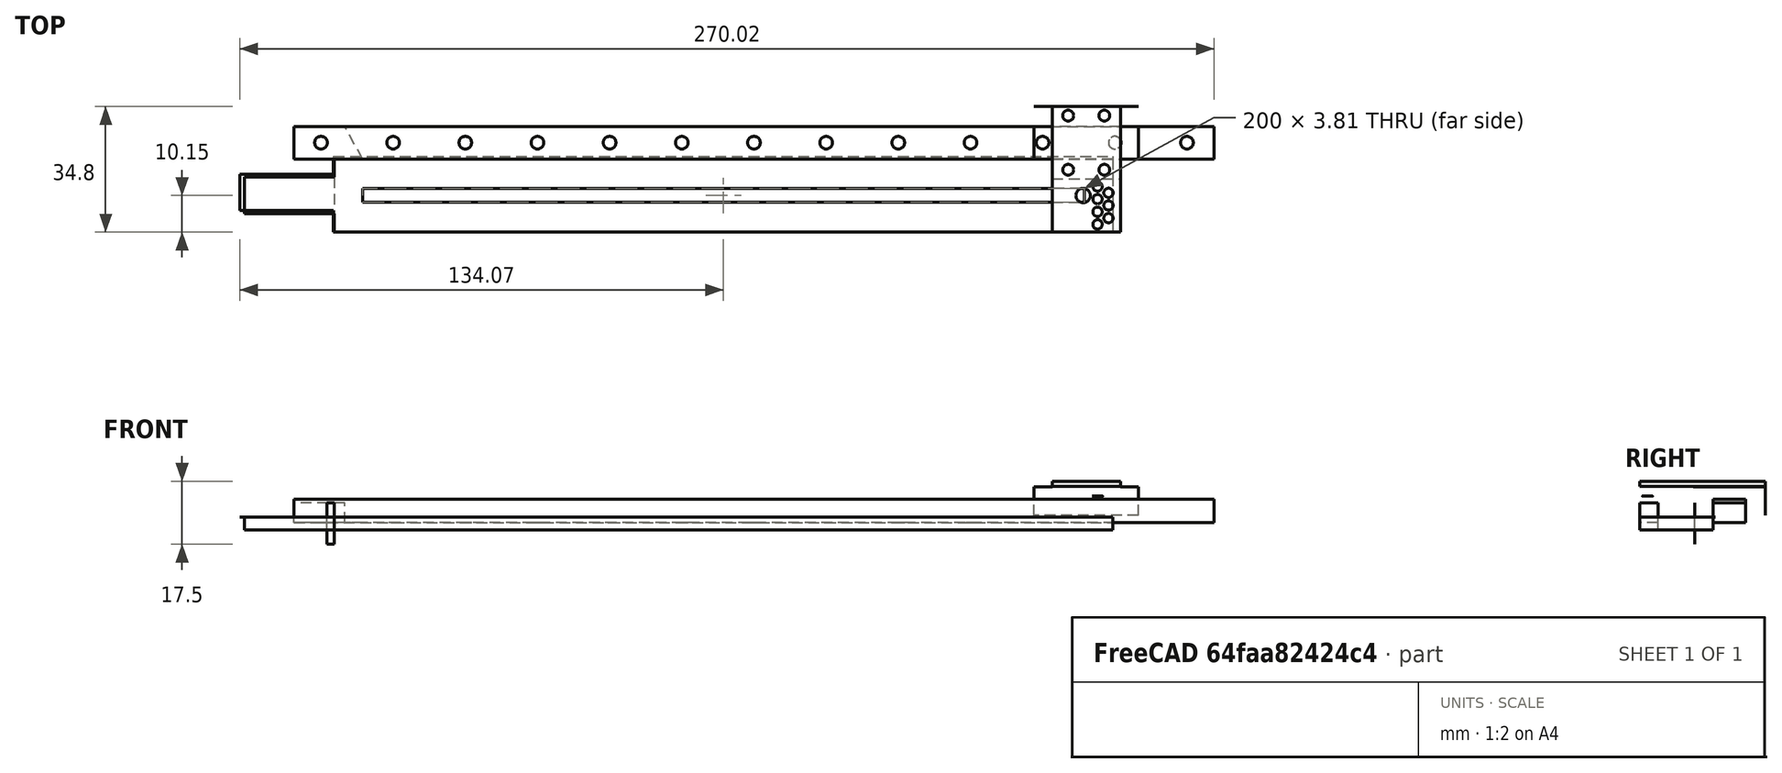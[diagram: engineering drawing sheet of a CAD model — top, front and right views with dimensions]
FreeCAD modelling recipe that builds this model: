
FCSTD DOCUMENT  (FreeCAD 0.21R33668 +26 (Git))
Label: v9
License: All rights reserved
LicenseURL: http://en.wikipedia.org/wiki/All_rights_reserved
objects: App::FeaturePython×73, Part::FeaturePython×54, App::Link×13
note: 53 computed .brp shape members not serialized (recipe doc carries the construction recipe); baked Part::Feature solids carry a one-line shape summary decoded from their .brp
EXTERNAL_REF file=parts/MG/mgn9c_13.FCStd obj=Body
EXTERNAL_REF file=parts/MG/mgn9c_slide.FCStd obj=Body001
EXTERNAL_REF file=parts/MagnetoPot/MagnetoPot.FCStd obj=Body
EXTERNAL_REF file=parts/NormalConnectorWithPin.FCStd obj=Body
EXTERNAL_REF file=parts/OmniballConnector/OmniballConnector_7945.FCStd obj=Body
EXTERNAL_REF file=parts/MagnetoPot/FlexBoard/FlexBoard_CAD.FCStd obj=Board_2da8
EXTERNAL_REF file=parts/BaseMagnetoPot.FCStd obj=Body

FEATURE [App::Link] Link  label="Rail"
  LinkedObject = -> <external parts/MG/mgn9c_13.FCStd>#Body
  _LinkOwner = 1895
FEATURE [App::Link] Link001  label="Slide"
  LinkPlacement = pos=(205.149,-5.5,2) rot=(0,0,1;0rad)
  LinkedObject = -> <external parts/MG/mgn9c_slide.FCStd>#Body001
  Placement = pos=(205.149,-5.5,2) rot=(0,0,1;0rad)
  _LinkOwner = 1895
FEATURE [App::Link] Link003  label="MP1_L_0200_103_5_ST"
  LinkPlacement = pos=(11.12,-20.3,-2) rot=(0,0,1;0rad)
  LinkedObject = -> <external parts/MagnetoPot/MagnetoPot.FCStd>#Body
  Placement = pos=(11.12,-20.3,-2) rot=(0,0,1;0rad)
  _LinkOwner = 1895
FEATURE [App::Link] Link005  label="SlideConnector"
  LinkPlacement = pos=(205.149,-5.5,2) rot=(0,0,1;0rad)
  LinkedObject = -> <external parts/NormalConnectorWithPin.FCStd>#Body
  Placement = pos=(205.149,-5.5,2) rot=(0,0,1;0rad)
  _LinkOwner = 1895
FEATURE [App::Link] Link006  label="7945"
  LinkPlacement = pos=(222.722,-18.15,8.1374) rot=(0,1,0;3.14159rad)
  LinkedObject = -> <external parts/OmniballConnector/OmniballConnector_7945.FCStd>#Body
  Placement = pos=(222.722,-18.15,8.1374) rot=(0,1,0;3.14159rad)
  _LinkOwner = 1895
FEATURE [App::Link] Link007  label="7945001"
  LinkPlacement = pos=(222.722,-14.65,8.1374) rot=(-1,0,0;3.14159rad)
  LinkedObject = -> <external parts/OmniballConnector/OmniballConnector_7945.FCStd>#Body
  Placement = pos=(222.722,-14.65,8.1374) rot=(-1,0,0;3.14159rad)
  _LinkOwner = 1895
FEATURE [App::Link] Link008  label="7945002"
  LinkPlacement = pos=(222.722,-11.15,8.1374) rot=(-1,0,0;3.14159rad)
  LinkedObject = -> <external parts/OmniballConnector/OmniballConnector_7945.FCStd>#Body
  Placement = pos=(222.722,-11.15,8.1374) rot=(-1,0,0;3.14159rad)
  _LinkOwner = 1895
FEATURE [App::Link] Link009  label="7945003"
  LinkPlacement = pos=(222.722,-7.65,8.1374) rot=(-1,0,0;3.14159rad)
  LinkedObject = -> <external parts/OmniballConnector/OmniballConnector_7945.FCStd>#Body
  Placement = pos=(222.722,-7.65,8.1374) rot=(-1,0,0;3.14159rad)
  _LinkOwner = 1895
FEATURE [App::Link] Link010  label="7945004"
  LinkPlacement = pos=(225.753,-16.4,8.1374) rot=(1,0,0;3.14159rad)
  LinkedObject = -> <external parts/OmniballConnector/OmniballConnector_7945.FCStd>#Body
  Placement = pos=(225.753,-16.4,8.1374) rot=(1,0,0;3.14159rad)
  _LinkOwner = 1895
FEATURE [App::Link] Link011  label="7945005"
  LinkPlacement = pos=(225.753,-9.4,8.1374) rot=(1,0,0;3.14159rad)
  LinkedObject = -> <external parts/OmniballConnector/OmniballConnector_7945.FCStd>#Body
  Placement = pos=(225.753,-9.4,8.1374) rot=(1,0,0;3.14159rad)
  _LinkOwner = 1895
FEATURE [App::Link] Link012  label="7945006"
  LinkPlacement = pos=(225.753,-12.9,8.1374) rot=(1,0,0;3.14159rad)
  LinkedObject = -> <external parts/OmniballConnector/OmniballConnector_7945.FCStd>#Body
  Placement = pos=(225.753,-12.9,8.1374) rot=(1,0,0;3.14159rad)
  _LinkOwner = 1895
FEATURE [App::Link] Link013  label="FlexBoard"
  LinkPlacement = pos=(25.38,-8.9,1.615) rot=(0,0,1;0rad)
  LinkedObject = -> <external parts/MagnetoPot/FlexBoard/FlexBoard_CAD.FCStd>#Board_2da8
  Placement = pos=(25.38,-8.9,1.615) rot=(0,0,1;0rad)
  _LinkOwner = 1895
FEATURE [App::Link] Link014  label="BaseMagentoPot"
  LinkPlacement = pos=(2.94885e-11,-3.58486e-11,-7.69447e-11) rot=(0,0,1;0rad)
  LinkedObject = -> <external parts/BaseMagnetoPot.FCStd>#Body
  Placement = pos=(2.94885e-11,-3.58486e-11,-7.69447e-11) rot=(0,0,1;0rad)
  _LinkOwner = 1895
FEATURE [Part::FeaturePython] Parts  # WARN: FeaturePython — macro-defined, semantics opaque (R4)
  Group = -> [Link,Link001,Link003,Link005,Link006,Link007,Link008,Link009,Link010,Link011,Link012,Link013,Link014]
  GroupMode = 0
FEATURE [App::FeaturePython] ElementLink  label="_Element"  # link proxy (typed FeaturePython)
  LinkTransform = true
  LinkedObject = -> _Element
  _Parent = -> Constraint
FEATURE [App::FeaturePython] Constraint  label="Locked"  # WARN: FeaturePython — macro-defined, semantics opaque (R4)
  Disabled = false
  Group = -> [ElementLink]
  _ConstraintType = 0
  _Parent = -> Constraints
FEATURE [App::FeaturePython] ElementLink001  label="_Element001"  # link proxy (typed FeaturePython)
  LinkTransform = true
  LinkedObject = -> _Element001
  _Parent = -> Constraint001
FEATURE [App::FeaturePython] ElementLink002  label="_Element002"  # link proxy (typed FeaturePython)
  LinkTransform = true
  LinkedObject = -> _Element002
  _Parent = -> Constraint001
FEATURE [App::FeaturePython] Constraint001  label="PlaneAlignment"  # WARN: FeaturePython — macro-defined, semantics opaque (R4)
  Angle = 0
  AnglePitch = 0
  AngleRoll = 0
  Cascade = false
  Disabled = false
  Group = -> [ElementLink001,ElementLink002]
  LockAngle = false
  _ConstraintType = 37
  _Parent = -> Constraints
FEATURE [App::FeaturePython] ElementLink003  label="_Element003"  # link proxy (typed FeaturePython)
  LinkTransform = true
  LinkedObject = -> _Element003
  _Parent = -> Constraint002
FEATURE [App::FeaturePython] ElementLink004  label="_Element"  # link proxy (typed FeaturePython)
  LinkTransform = true
  LinkedObject = -> _Element
  _Parent = -> Constraint002
FEATURE [App::FeaturePython] Constraint002  label="PlaneAlignment001"  # WARN: FeaturePython — macro-defined, semantics opaque (R4)
  Angle = 0
  AnglePitch = 0
  AngleRoll = 0
  Cascade = false
  Disabled = false
  Group = -> [ElementLink003,ElementLink004]
  LockAngle = false
  _ConstraintType = 37
  _Parent = -> Constraints
FEATURE [App::FeaturePython] ElementLink023  label="_Element020"  # link proxy (typed FeaturePython)
  LinkTransform = true
  LinkedObject = -> _Element020
  _Parent = -> Constraint012
FEATURE [App::FeaturePython] ElementLink024  label="_Element021"  # link proxy (typed FeaturePython)
  LinkTransform = true
  LinkedObject = -> _Element021
  _Parent = -> Constraint012
FEATURE [App::FeaturePython] Constraint012  label="PlaneAlignment011"  # WARN: FeaturePython — macro-defined, semantics opaque (R4)
  Angle = 0
  AnglePitch = 0
  AngleRoll = 0
  Cascade = false
  Disabled = false
  Group = -> [ElementLink023,ElementLink024]
  LockAngle = false
  _ConstraintType = 37
  _Parent = -> Constraints
FEATURE [App::FeaturePython] ElementLink025  label="_Element022"  # link proxy (typed FeaturePython)
  LinkTransform = true
  LinkedObject = -> _Element022
  _Parent = -> Constraint013
FEATURE [App::FeaturePython] ElementLink026  label="_Element023"  # link proxy (typed FeaturePython)
  LinkTransform = true
  LinkedObject = -> _Element023
  _Parent = -> Constraint013
FEATURE [App::FeaturePython] Constraint013  label="PlaneAlignment012"  # WARN: FeaturePython — macro-defined, semantics opaque (R4)
  Angle = 0
  AnglePitch = 0
  AngleRoll = 0
  Cascade = false
  Disabled = false
  Group = -> [ElementLink025,ElementLink026]
  LockAngle = false
  _ConstraintType = 37
  _Parent = -> Constraints
FEATURE [App::FeaturePython] ElementLink027  label="_Element024"  # link proxy (typed FeaturePython)
  LinkTransform = true
  LinkedObject = -> _Element024
  _Parent = -> Constraint014
FEATURE [App::FeaturePython] ElementLink028  label="_Element025"  # link proxy (typed FeaturePython)
  LinkTransform = true
  LinkedObject = -> _Element025
  _Parent = -> Constraint014
FEATURE [App::FeaturePython] Constraint014  label="PlaneAlignment013"  # WARN: FeaturePython — macro-defined, semantics opaque (R4)
  Angle = 0
  AnglePitch = 0
  AngleRoll = 0
  Cascade = false
  Disabled = false
  Group = -> [ElementLink027,ElementLink028]
  LockAngle = false
  _ConstraintType = 37
  _Parent = -> Constraints
FEATURE [App::FeaturePython] ElementLink029  label="_Element030"  # link proxy (typed FeaturePython)
  LinkTransform = true
  LinkedObject = -> _Element030
  _Parent = -> Constraint015
FEATURE [App::FeaturePython] ElementLink030  label="_Element031"  # link proxy (typed FeaturePython)
  LinkTransform = true
  LinkedObject = -> _Element031
  _Parent = -> Constraint015
FEATURE [App::FeaturePython] Constraint015  label="PlaneCoincident"  # WARN: FeaturePython — macro-defined, semantics opaque (R4)
  Angle = 0
  AnglePitch = 0
  AngleRoll = 0
  Cascade = false
  Disabled = false
  Group = -> [ElementLink029,ElementLink030]
  LockAngle = false
  Multiply = false
  OffsetX = 0
  OffsetY = 0
  _ConstraintType = 35
  _Parent = -> Constraints
FEATURE [App::FeaturePython] ElementLink031  label="_Element032"  # link proxy (typed FeaturePython)
  LinkTransform = true
  LinkedObject = -> _Element032
  _Parent = -> Constraint016
FEATURE [App::FeaturePython] ElementLink032  label="_Element033"  # link proxy (typed FeaturePython)
  LinkTransform = true
  LinkedObject = -> _Element033
  _Parent = -> Constraint016
FEATURE [App::FeaturePython] Constraint016  label="PlaneCoincident001"  # WARN: FeaturePython — macro-defined, semantics opaque (R4)
  Angle = 0
  AnglePitch = 0
  AngleRoll = 0
  Cascade = false
  Disabled = false
  Group = -> [ElementLink031,ElementLink032]
  LockAngle = false
  Multiply = false
  OffsetX = 0
  OffsetY = 0
  _ConstraintType = 35
  _Parent = -> Constraints
FEATURE [App::FeaturePython] ElementLink033  label="_Element034"  # link proxy (typed FeaturePython)
  LinkTransform = true
  LinkedObject = -> _Element034
  _Parent = -> Constraint017
FEATURE [App::FeaturePython] ElementLink034  label="_Element035"  # link proxy (typed FeaturePython)
  LinkTransform = true
  LinkedObject = -> _Element035
  _Parent = -> Constraint017
FEATURE [App::FeaturePython] Constraint017  label="PlaneCoincident002"  # WARN: FeaturePython — macro-defined, semantics opaque (R4)
  Angle = 0
  AnglePitch = 0
  AngleRoll = 0
  Cascade = false
  Disabled = false
  Group = -> [ElementLink033,ElementLink034]
  LockAngle = false
  Multiply = false
  OffsetX = 0
  OffsetY = 0
  _ConstraintType = 35
  _Parent = -> Constraints
FEATURE [App::FeaturePython] ElementLink035  label="_Element036"  # link proxy (typed FeaturePython)
  LinkTransform = true
  LinkedObject = -> _Element036
  _Parent = -> Constraint018
FEATURE [App::FeaturePython] ElementLink036  label="_Element037"  # link proxy (typed FeaturePython)
  LinkTransform = true
  LinkedObject = -> _Element037
  _Parent = -> Constraint018
FEATURE [App::FeaturePython] Constraint018  label="PlaneCoincident003"  # WARN: FeaturePython — macro-defined, semantics opaque (R4)
  Angle = 0
  AnglePitch = 0
  AngleRoll = 0
  Cascade = false
  Disabled = false
  Group = -> [ElementLink035,ElementLink036]
  LockAngle = false
  Multiply = false
  OffsetX = 0
  OffsetY = 0
  _ConstraintType = 35
  _Parent = -> Constraints
FEATURE [App::FeaturePython] ElementLink037  label="_Element038"  # link proxy (typed FeaturePython)
  LinkTransform = true
  LinkedObject = -> _Element038
  _Parent = -> Constraint019
FEATURE [App::FeaturePython] ElementLink038  label="_Element039"  # link proxy (typed FeaturePython)
  LinkTransform = true
  LinkedObject = -> _Element039
  _Parent = -> Constraint019
FEATURE [App::FeaturePython] Constraint019  label="PlaneCoincident004"  # WARN: FeaturePython — macro-defined, semantics opaque (R4)
  Angle = 0
  AnglePitch = 0
  AngleRoll = 0
  Cascade = false
  Disabled = false
  Group = -> [ElementLink037,ElementLink038]
  LockAngle = false
  Multiply = false
  OffsetX = 0
  OffsetY = 0
  _ConstraintType = 35
  _Parent = -> Constraints
FEATURE [App::FeaturePython] ElementLink039  label="_Element040"  # link proxy (typed FeaturePython)
  LinkTransform = true
  LinkedObject = -> _Element040
  _Parent = -> Constraint020
FEATURE [App::FeaturePython] ElementLink040  label="_Element041"  # link proxy (typed FeaturePython)
  LinkTransform = true
  LinkedObject = -> _Element041
  _Parent = -> Constraint020
FEATURE [App::FeaturePython] Constraint020  label="PlaneCoincident005"  # WARN: FeaturePython — macro-defined, semantics opaque (R4)
  Angle = 0
  AnglePitch = 0
  AngleRoll = 0
  Cascade = false
  Disabled = false
  Group = -> [ElementLink039,ElementLink040]
  LockAngle = false
  Multiply = false
  OffsetX = 0
  OffsetY = 0
  _ConstraintType = 35
  _Parent = -> Constraints
FEATURE [App::FeaturePython] ElementLink041  label="_Element042"  # link proxy (typed FeaturePython)
  LinkTransform = true
  LinkedObject = -> _Element042
  _Parent = -> Constraint021
FEATURE [App::FeaturePython] ElementLink042  label="_Element043"  # link proxy (typed FeaturePython)
  LinkTransform = true
  LinkedObject = -> _Element043
  _Parent = -> Constraint021
FEATURE [App::FeaturePython] Constraint021  label="PlaneCoincident006"  # WARN: FeaturePython — macro-defined, semantics opaque (R4)
  Angle = 0
  AnglePitch = 0
  AngleRoll = 0
  Cascade = false
  Disabled = false
  Group = -> [ElementLink041,ElementLink042]
  LockAngle = false
  Multiply = false
  OffsetX = 0
  OffsetY = 0
  _ConstraintType = 35
  _Parent = -> Constraints
FEATURE [App::FeaturePython] Constraints  # WARN: FeaturePython — macro-defined, semantics opaque (R4)
  Group = -> [Constraint,Constraint001,Constraint002,Constraint012,Constraint013,Constraint014,Constraint015,Constraint016,Constraint017,Constraint018,Constraint019,Constraint020,Constraint021,Constraint024,Constraint026,Constraint027,Constraint028,Constraint029,Constraint030,Constraint031,Constraint032,Constraint033,Constraint034,Constraint035]
  _Version = 1
FEATURE [Part::FeaturePython] _Element  # link proxy (typed FeaturePython)
  Detach = false
  LinkTransform = true
  LinkedObject = -> Link [LinearPattern.Face5]
  _Parent = -> Elements
FEATURE [Part::FeaturePython] _Element001  # link proxy (typed FeaturePython)
  Detach = false
  LinkTransform = true
  LinkedObject = -> Link001 [Pocket003.Face12]
  _Parent = -> Elements
FEATURE [Part::FeaturePython] _Element002  # link proxy (typed FeaturePython)
  Detach = false
  LinkTransform = true
  LinkedObject = -> Link [LinearPattern.Face6]
  _Parent = -> Elements
FEATURE [Part::FeaturePython] _Element003  # link proxy (typed FeaturePython)
  Detach = false
  LinkTransform = true
  LinkedObject = -> Link001 [Pocket003.Face11]
  _Parent = -> Elements
FEATURE [Part::FeaturePython] _Element005  # link proxy (typed FeaturePython)
  Detach = false
  LinkTransform = true
  LinkedObject = -> Link [LinearPattern.Face2]
  _Parent = -> Elements
FEATURE [Part::FeaturePython] _Element008  # link proxy (typed FeaturePython)
  Detach = false
  LinkTransform = true
  LinkedObject = -> Link [LinearPattern.Face4]
  _Parent = -> Elements
FEATURE [Part::FeaturePython] _Element009  # link proxy (typed FeaturePython)
  Detach = false
  LinkTransform = true
  LinkedObject = -> Link003 [Pad.Face13]
  _Parent = -> Elements
FEATURE [Part::FeaturePython] _Element012  # link proxy (typed FeaturePython)
  Detach = false
  LinkTransform = true
  LinkedObject = -> Link003 [Pad.Face5]
  _Parent = -> Elements
FEATURE [Part::FeaturePython] _Element013  # link proxy (typed FeaturePython)
  Detach = false
  LinkTransform = true
  LinkedObject = -> Link003 [Pad.Face8]
  _Parent = -> Elements
FEATURE [Part::FeaturePython] _Element016  # link proxy (typed FeaturePython)
  Detach = false
  LinkTransform = true
  LinkedObject = -> Link003 [Pad.Face14]
  _Parent = -> Elements
FEATURE [Part::FeaturePython] _Element020  # link proxy (typed FeaturePython)
  Detach = false
  LinkTransform = true
  LinkedObject = -> Link005 [Pocket002.Face4]
  _Parent = -> Elements
FEATURE [Part::FeaturePython] _Element021  # link proxy (typed FeaturePython)
  Detach = false
  LinkTransform = true
  LinkedObject = -> Link001 [Pocket003.Face6]
  _Parent = -> Elements
FEATURE [Part::FeaturePython] _Element022  # link proxy (typed FeaturePython)
  Detach = false
  LinkTransform = true
  LinkedObject = -> Link005 [Pocket002.Face1]
  _Parent = -> Elements
FEATURE [Part::FeaturePython] _Element023  # link proxy (typed FeaturePython)
  Detach = false
  LinkTransform = true
  LinkedObject = -> Link001 [Pocket003.Face14]
  _Parent = -> Elements
FEATURE [Part::FeaturePython] _Element024  # link proxy (typed FeaturePython)
  Detach = false
  LinkTransform = true
  LinkedObject = -> Link005 [Pocket002.Face2]
  _Parent = -> Elements
FEATURE [Part::FeaturePython] _Element025  # link proxy (typed FeaturePython)
  Detach = false
  LinkTransform = true
  LinkedObject = -> Link001 [Pocket003.Face7]
  _Parent = -> Elements
FEATURE [Part::FeaturePython] _Element026  # link proxy (typed FeaturePython)
  Detach = false
  LinkTransform = true
  LinkedObject = -> Link006 [Revolution.Face3]
  _Parent = -> Elements
FEATURE [Part::FeaturePython] _Element027  # link proxy (typed FeaturePython)
  Detach = false
  LinkTransform = true
  LinkedObject = -> Link005 [Pocket002.Face5]
  _Parent = -> Elements
FEATURE [Part::FeaturePython] _Element028  # link proxy (typed FeaturePython)
  Detach = false
  LinkTransform = true
  LinkedObject = -> Link006 [Revolution.Vertex2]
  _Parent = -> Elements
FEATURE [Part::FeaturePython] _Element029  # link proxy (typed FeaturePython)
  Detach = false
  LinkTransform = true
  LinkedObject = -> Link005 [Pocket002.Edge20]
  _Parent = -> Elements
FEATURE [Part::FeaturePython] _Element030  # link proxy (typed FeaturePython)
  Detach = false
  LinkTransform = true
  LinkedObject = -> Link006 [Revolution.Edge3]
  _Parent = -> Elements
FEATURE [Part::FeaturePython] _Element031  # link proxy (typed FeaturePython)
  Detach = false
  LinkTransform = true
  LinkedObject = -> Link005 [Pocket003.Edge40]
  _Parent = -> Elements
FEATURE [Part::FeaturePython] _Element032  # link proxy (typed FeaturePython)
  Detach = false
  LinkTransform = true
  LinkedObject = -> Link007 [Revolution.Edge3]
  _Parent = -> Elements
FEATURE [Part::FeaturePython] _Element033  # link proxy (typed FeaturePython)
  Detach = false
  LinkTransform = true
  LinkedObject = -> Link005 [Pocket003.Edge42]
  _Parent = -> Elements
FEATURE [Part::FeaturePython] _Element034  # link proxy (typed FeaturePython)
  Detach = false
  LinkTransform = true
  LinkedObject = -> Link008 [Revolution.Edge3]
  _Parent = -> Elements
FEATURE [Part::FeaturePython] _Element035  # link proxy (typed FeaturePython)
  Detach = false
  LinkTransform = true
  LinkedObject = -> Link005 [Pocket003.Edge44]
  _Parent = -> Elements
FEATURE [Part::FeaturePython] _Element036  # link proxy (typed FeaturePython)
  Detach = false
  LinkTransform = true
  LinkedObject = -> Link009 [Revolution.Edge3]
  _Parent = -> Elements
FEATURE [Part::FeaturePython] _Element037  # link proxy (typed FeaturePython)
  Detach = false
  LinkTransform = true
  LinkedObject = -> Link005 [Pocket003.Edge46]
  _Parent = -> Elements
FEATURE [Part::FeaturePython] _Element038  # link proxy (typed FeaturePython)
  Detach = false
  LinkTransform = true
  LinkedObject = -> Link005 [Pocket003.Edge41]
  _Parent = -> Elements
FEATURE [Part::FeaturePython] _Element039  # link proxy (typed FeaturePython)
  Detach = false
  LinkTransform = true
  LinkedObject = -> Link010 [Revolution.Edge3]
  _Parent = -> Elements
FEATURE [Part::FeaturePython] _Element040  # link proxy (typed FeaturePython)
  Detach = false
  LinkTransform = true
  LinkedObject = -> Link011 [Revolution.Edge3]
  _Parent = -> Elements
FEATURE [Part::FeaturePython] _Element041  # link proxy (typed FeaturePython)
  Detach = false
  LinkTransform = true
  LinkedObject = -> Link005 [Pocket003.Edge47]
  _Parent = -> Elements
FEATURE [Part::FeaturePython] _Element042  # link proxy (typed FeaturePython)
  Detach = false
  LinkTransform = true
  LinkedObject = -> Link012 [Revolution.Edge3]
  _Parent = -> Elements
FEATURE [Part::FeaturePython] _Element043  # link proxy (typed FeaturePython)
  Detach = false
  LinkTransform = true
  LinkedObject = -> Link005 [Pocket003.Edge45]
  _Parent = -> Elements
FEATURE [App::FeaturePython] Elements  # WARN: FeaturePython — macro-defined, semantics opaque (R4)
  Group = -> [_Element,_Element001,_Element002,_Element003,_Element005,_Element008,_Element009,_Element012,_Element013,_Element016,_Element020,_Element021,_Element022,_Element023,_Element024,_Element025,_Element026,_Element027,_Element028,_Element029,_Element030,_Element031,_Element032,_Element033,_Element034,_Element035,_Element036,_Element037,_Element038,_Element039,_Element040,_Element041,_Element042,+19 more]
FEATURE [Part::FeaturePython] Assembly  # WARN: FeaturePython — macro-defined, semantics opaque (R4)
  AutoRelax = true
  BuildShape = 0
  Freeze = false
  Group = -> [Constraints,Elements,Parts]
  Verbose = false
  _SolverType = 1
  _Version = 1
FEATURE [Part::FeaturePython] _Element044  # link proxy (typed FeaturePython)
  Detach = false
  LinkTransform = true
  LinkedObject = -> Link013 [Board_Geoms_2da8.Pcb_2da8.Face10]
  _Parent = -> Elements
FEATURE [Part::FeaturePython] _Element045  # link proxy (typed FeaturePython)
  Detach = false
  LinkTransform = true
  LinkedObject = -> Link013 [Board_Geoms_2da8.Pcb_2da8.Face4]
  _Parent = -> Elements
FEATURE [App::FeaturePython] Constraint024  label="PlaneAlignment016"  # WARN: FeaturePython — macro-defined, semantics opaque (R4)
  Angle = 0
  AnglePitch = 0
  AngleRoll = 0
  Cascade = false
  Disabled = false
  Group = -> [ElementLink047,ElementLink048]
  LockAngle = false
  _ConstraintType = 37
  _Parent = -> Constraints
FEATURE [App::FeaturePython] ElementLink047  label="_Element046"  # link proxy (typed FeaturePython)
  LinkTransform = true
  LinkedObject = -> _Element046
  _Parent = -> Constraint024
FEATURE [Part::FeaturePython] _Element046  # link proxy (typed FeaturePython)
  Detach = false
  LinkTransform = true
  LinkedObject = -> Link003 [Pad.Face4]
  _Parent = -> Elements
FEATURE [App::FeaturePython] ElementLink048  label="_Element047"  # link proxy (typed FeaturePython)
  LinkTransform = true
  LinkedObject = -> _Element047
  _Parent = -> Constraint024
FEATURE [Part::FeaturePython] _Element047  # link proxy (typed FeaturePython)
  Detach = false
  LinkTransform = true
  LinkedObject = -> Link [LinearPattern.Face1]
  _Parent = -> Elements
FEATURE [Part::FeaturePython] _Element048  # link proxy (typed FeaturePython)
  Detach = false
  LinkTransform = true
  LinkedObject = -> Link013 [Board_Geoms_2da8.Pcb_2da8.Face1]
  _Parent = -> Elements
FEATURE [Part::FeaturePython] _Element049  # link proxy (typed FeaturePython)
  Detach = false
  LinkTransform = true
  LinkedObject = -> Link003 [Pad.Face7]
  _Parent = -> Elements
FEATURE [App::FeaturePython] Constraint026  label="SameOrientation"  # WARN: FeaturePython — macro-defined, semantics opaque (R4)
  Disabled = false
  Group = -> [ElementLink051,ElementLink052]
  _ConstraintType = 2
  _Parent = -> Constraints
FEATURE [App::FeaturePython] ElementLink051  label="_Element009"  # link proxy (typed FeaturePython)
  LinkTransform = true
  LinkedObject = -> _Element009
  _Parent = -> Constraint026
FEATURE [App::FeaturePython] ElementLink052  label="_Element008"  # link proxy (typed FeaturePython)
  LinkTransform = true
  LinkedObject = -> _Element008
  _Parent = -> Constraint026
FEATURE [App::FeaturePython] Constraint027  label="PlaneAlignment018"  # WARN: FeaturePython — macro-defined, semantics opaque (R4)
  Angle = 0
  AnglePitch = 0
  AngleRoll = 0
  Cascade = false
  Disabled = false
  Group = -> [ElementLink053,ElementLink054]
  LockAngle = false
  _ConstraintType = 37
  _Parent = -> Constraints
FEATURE [App::FeaturePython] ElementLink053  label="_Element050"  # link proxy (typed FeaturePython)
  LinkTransform = true
  LinkedObject = -> _Element050
  _Parent = -> Constraint027
FEATURE [Part::FeaturePython] _Element050  # link proxy (typed FeaturePython)
  Detach = false
  LinkTransform = true
  LinkedObject = -> Link014 [Pocket001.Face32]
  _Parent = -> Elements
FEATURE [App::FeaturePython] ElementLink054  label="_Element005"  # link proxy (typed FeaturePython)
  LinkTransform = true
  LinkedObject = -> _Element005
  _Parent = -> Constraint027
FEATURE [App::FeaturePython] Constraint028  label="PlaneAlignment019"  # WARN: FeaturePython — macro-defined, semantics opaque (R4)
  Angle = 0
  AnglePitch = 0
  AngleRoll = 0
  Cascade = false
  Disabled = false
  Group = -> [ElementLink055,ElementLink056]
  LockAngle = false
  _ConstraintType = 37
  _Parent = -> Constraints
FEATURE [App::FeaturePython] ElementLink055  label="_Element051"  # link proxy (typed FeaturePython)
  LinkTransform = true
  LinkedObject = -> _Element051
  _Parent = -> Constraint028
FEATURE [Part::FeaturePython] _Element051  # link proxy (typed FeaturePython)
  Detach = false
  LinkTransform = true
  LinkedObject = -> Link014 [Pocket001.Face31]
  _Parent = -> Elements
FEATURE [App::FeaturePython] ElementLink056  label="_Element002"  # link proxy (typed FeaturePython)
  LinkTransform = true
  LinkedObject = -> _Element002
  _Parent = -> Constraint028
FEATURE [App::FeaturePython] Constraint029  label="PlaneAlignment020"  # WARN: FeaturePython — macro-defined, semantics opaque (R4)
  Angle = 0
  AnglePitch = 0
  AngleRoll = 0
  Cascade = false
  Disabled = false
  Group = -> [ElementLink057,ElementLink058]
  LockAngle = false
  _ConstraintType = 37
  _Parent = -> Constraints
FEATURE [App::FeaturePython] ElementLink057  label="_Element052"  # link proxy (typed FeaturePython)
  LinkTransform = true
  LinkedObject = -> _Element052
  _Parent = -> Constraint029
FEATURE [Part::FeaturePython] _Element052  # link proxy (typed FeaturePython)
  Detach = false
  LinkTransform = true
  LinkedObject = -> Link014 [Pocket001.Face24]
  _Parent = -> Elements
FEATURE [App::FeaturePython] ElementLink058  label="_Element008"  # link proxy (typed FeaturePython)
  LinkTransform = true
  LinkedObject = -> _Element008
  _Parent = -> Constraint029
FEATURE [App::FeaturePython] Constraint030  label="PlaneAlignment021"  # WARN: FeaturePython — macro-defined, semantics opaque (R4)
  Angle = 0
  AnglePitch = 0
  AngleRoll = 0
  Cascade = false
  Disabled = false
  Group = -> [ElementLink059,ElementLink060]
  LockAngle = false
  _ConstraintType = 37
  _Parent = -> Constraints
FEATURE [App::FeaturePython] ElementLink059  label="_Element053"  # link proxy (typed FeaturePython)
  LinkTransform = true
  LinkedObject = -> _Element053
  _Parent = -> Constraint030
FEATURE [Part::FeaturePython] _Element053  # link proxy (typed FeaturePython)
  Detach = false
  LinkTransform = true
  LinkedObject = -> Link003 [Pad.Face1]
  _Parent = -> Elements
FEATURE [App::FeaturePython] ElementLink060  label="_Element054"  # link proxy (typed FeaturePython)
  LinkTransform = true
  LinkedObject = -> _Element054
  _Parent = -> Constraint030
FEATURE [Part::FeaturePython] _Element054  # link proxy (typed FeaturePython)
  Detach = false
  LinkTransform = true
  LinkedObject = -> Link014 [Pocket001.Face4]
  _Parent = -> Elements
FEATURE [App::FeaturePython] Constraint031  label="PlaneAlignment022"  # WARN: FeaturePython — macro-defined, semantics opaque (R4)
  Angle = 0
  AnglePitch = 0
  AngleRoll = 0
  Cascade = false
  Disabled = false
  Group = -> [ElementLink061,ElementLink062]
  LockAngle = false
  _ConstraintType = 37
  _Parent = -> Constraints
FEATURE [App::FeaturePython] ElementLink061  label="_Element055"  # link proxy (typed FeaturePython)
  LinkTransform = true
  LinkedObject = -> _Element055
  _Parent = -> Constraint031
FEATURE [Part::FeaturePython] _Element055  # link proxy (typed FeaturePython)
  Detach = false
  LinkTransform = true
  LinkedObject = -> Link003 [Pad.Face6]
  _Parent = -> Elements
FEATURE [App::FeaturePython] ElementLink062  label="_Element056"  # link proxy (typed FeaturePython)
  LinkTransform = true
  LinkedObject = -> _Element056
  _Parent = -> Constraint031
FEATURE [Part::FeaturePython] _Element056  # link proxy (typed FeaturePython)
  Detach = false
  LinkTransform = true
  LinkedObject = -> Link014 [Pocket001.Face10]
  _Parent = -> Elements
FEATURE [App::FeaturePython] Constraint032  label="PlaneAlignment023"  # WARN: FeaturePython — macro-defined, semantics opaque (R4)
  Angle = 0
  AnglePitch = 0
  AngleRoll = 0
  Cascade = false
  Disabled = false
  Group = -> [ElementLink063,ElementLink064]
  LockAngle = false
  _ConstraintType = 37
  _Parent = -> Constraints
FEATURE [App::FeaturePython] ElementLink063  label="_Element009"  # link proxy (typed FeaturePython)
  LinkTransform = true
  LinkedObject = -> _Element009
  _Parent = -> Constraint032
FEATURE [App::FeaturePython] ElementLink064  label="_Element057"  # link proxy (typed FeaturePython)
  LinkTransform = true
  LinkedObject = -> _Element057
  _Parent = -> Constraint032
FEATURE [Part::FeaturePython] _Element057  # link proxy (typed FeaturePython)
  Detach = false
  LinkTransform = true
  LinkedObject = -> Link014 [Pocket001.Face8]
  _Parent = -> Elements
FEATURE [App::FeaturePython] Constraint033  label="PlaneAlignment024"  # WARN: FeaturePython — macro-defined, semantics opaque (R4)
  Angle = 0
  AnglePitch = 0
  AngleRoll = 0
  Cascade = false
  Disabled = false
  Group = -> [ElementLink065,ElementLink066]
  LockAngle = false
  _ConstraintType = 37
  _Parent = -> Constraints
FEATURE [App::FeaturePython] ElementLink065  label="_Element058"  # link proxy (typed FeaturePython)
  LinkTransform = true
  LinkedObject = -> _Element058
  _Parent = -> Constraint033
FEATURE [Part::FeaturePython] _Element058  # link proxy (typed FeaturePython)
  Detach = false
  LinkTransform = true
  LinkedObject = -> Link013 [Board_Geoms_2da8.Pcb_2da8.Face7]
  _Parent = -> Elements
FEATURE [App::FeaturePython] ElementLink066  label="_Element059"  # link proxy (typed FeaturePython)
  LinkTransform = true
  LinkedObject = -> _Element059
  _Parent = -> Constraint033
FEATURE [Part::FeaturePython] _Element059  # link proxy (typed FeaturePython)
  Detach = false
  LinkTransform = true
  LinkedObject = -> Link003 [Pad.Face3]
  _Parent = -> Elements
FEATURE [App::FeaturePython] Constraint034  label="PlaneAlignment025"  # WARN: FeaturePython — macro-defined, semantics opaque (R4)
  Angle = 0
  AnglePitch = 0
  AngleRoll = 0
  Cascade = false
  Disabled = false
  Group = -> [ElementLink067,ElementLink068]
  LockAngle = false
  _ConstraintType = 37
  _Parent = -> Constraints
FEATURE [App::FeaturePython] ElementLink067  label="_Element060"  # link proxy (typed FeaturePython)
  LinkTransform = true
  LinkedObject = -> _Element060
  _Parent = -> Constraint034
FEATURE [Part::FeaturePython] _Element060  # link proxy (typed FeaturePython)
  Detach = false
  LinkTransform = true
  LinkedObject = -> Link013 [Board_Geoms_2da8.Pcb_2da8.Face6]
  _Parent = -> Elements
FEATURE [App::FeaturePython] ElementLink068  label="_Element061"  # link proxy (typed FeaturePython)
  LinkTransform = true
  LinkedObject = -> _Element061
  _Parent = -> Constraint034
FEATURE [Part::FeaturePython] _Element061  # link proxy (typed FeaturePython)
  Detach = false
  LinkTransform = true
  LinkedObject = -> Link003 [Pad.Face2]
  _Parent = -> Elements
FEATURE [App::FeaturePython] Constraint035  label="PlaneAlignment026"  # WARN: FeaturePython — macro-defined, semantics opaque (R4)
  Angle = 0
  AnglePitch = 0
  AngleRoll = 0
  Cascade = false
  Disabled = false
  Group = -> [ElementLink069,ElementLink070]
  LockAngle = false
  _ConstraintType = 37
  _Parent = -> Constraints
FEATURE [App::FeaturePython] ElementLink069  label="_Element044"  # link proxy (typed FeaturePython)
  LinkTransform = true
  LinkedObject = -> _Element044
  _Parent = -> Constraint035
FEATURE [App::FeaturePython] ElementLink070  label="_Element016"  # link proxy (typed FeaturePython)
  LinkTransform = true
  LinkedObject = -> _Element016
  _Parent = -> Constraint035

RESOLVED EXTERNAL PARTS (link-assembly join: the EXTERNAL_REF files above that resolve inside this repo's crawl, each included once):
---- part parts/BaseMagnetoPot.FCStd = doc fcstd_0771cd1a7cab ----
FCSTD DOCUMENT  (FreeCAD 0.21R33668 +26 (Git))
Label: BaseMagnetoPot
License: All rights reserved
LicenseURL: http://en.wikipedia.org/wiki/All_rights_reserved
objects: Sketcher::SketchObject×10, PartDesign::Pocket×5, PartDesign::Pad×4, PartDesign::SubShapeBinder×2, PartDesign::Body×2
note: 32 computed .brp shape members not serialized (recipe doc carries the construction recipe); baked Part::Feature solids carry a one-line shape summary decoded from their .brp
EXTERNAL_REF file=MG/Datasheet.FCStd obj=Spreadsheet
EXTERNAL_REF file=MG/mgn9c_13.FCStd obj=Body
EXTERNAL_REF file=MagnetoPot/MagnetoPot.FCStd obj=Body
EXTERNAL_REF file=MG/mgn9c_13.FCStd obj=Sketch

FEATURE [PartDesign::SubShapeBinder] Binder  label="Rail"
  BindCopyOnChange = 0
  BindMode = 0
  ClaimChildren = false
  Context = -> Body [Binder.]
  Fuse = false
  MakeFace = true
  OffsetFill = false
  OffsetIntersection = false
  OffsetJoinType = 0
  OffsetOpenResult = false
  PartialLoad = false
  Relative = true
  Support = -> [<external MG/mgn9c_13.FCStd>#Body]
  _Version = 2
FEATURE [Sketcher::SketchObject] Sketch
  ExternalGeometry = -> [Binder]
  FullyConstrained = true
  MapMode = 5
  Support = -> [XY_Plane]
  expr: .Constraints.EndStopToActiveDistance = (<<Datasheet>>#<<mgn9c>>.Dim_L - <<Datasheet>>#<<mgn9c>>.Dim_L1) / 2
  expr: .Constraints.PartWidth = 20.3
  expr: .Constraints.TravelDistance = 200 mm + <<Datasheet>>#<<mgn9c>>.Dim_L - 2 mm
  expr: Constraints[25] = <<Datasheet>>#<<mgn9c>>.Dim_L
  sketch-geometry (23):
    g0: Circle CenterX=7.5 CenterY=4.5 CenterZ=0 NormalX=0 NormalY=0 NormalZ=1 AngleXU=0 Radius=1.75
    g1: LineSegment StartX=0 StartY=0 StartZ=0 EndX=14.05 EndY=0 EndZ=0
    g2: LineSegment StartX=14.05 StartY=0 StartZ=0 EndX=14.05 EndY=9 EndZ=0
    g3: LineSegment StartX=14.05 StartY=9 StartZ=0 EndX=0 EndY=9 EndZ=0
    g4: LineSegment StartX=0 StartY=9 StartZ=0 EndX=0 EndY=0 EndZ=0
    g5: GeomPoint X=127.5 Y=9 Z=0
    g6: GeomPoint X=240.95 Y=9 Z=0
    g7: GeomPoint X=7.5 Y=6.25 Z=0
    g8: LineSegment StartX=14.05 StartY=9 StartZ=0 EndX=19.05 EndY=9 EndZ=0
    g9: LineSegment StartX=19.05 StartY=0 StartZ=0 EndX=14.05 EndY=9 EndZ=0
    g10: GeomPoint X=219.05 Y=0 Z=0
    g11: GeomPoint X=212.05 Y=9 Z=0
    g12: GeomPoint X=119.05 Y=0 Z=0
    g13: GeomPoint X=11.12 Y=0 Z=0
    g14: GeomPoint X=226.98 Y=0 Z=0
    g15: LineSegment StartX=19.05 StartY=0 StartZ=0 EndX=19.05 EndY=-20.3 EndZ=0
    g16: LineSegment StartX=11.12 StartY=-20.3 StartZ=0 EndX=19.05 EndY=-20.3 EndZ=0
    g17: LineSegment StartX=11.12 StartY=0 StartZ=0 EndX=11.12 EndY=-20.3 EndZ=0
    g18: GeomPoint X=0 Y=0 Z=0
    g19: GeomPoint X=11.12 Y=0 Z=0
    g20: GeomPoint X=0 Y=0 Z=0
    g21: GeomPoint X=11.12 Y=0 Z=0
    g22: LineSegment StartX=0 StartY=0 StartZ=0 EndX=11.12 EndY=0 EndZ=0
  constraints (49):
    c: Coincident(g0,g-5)
    c: Coincident(g1,g2)
    c: Coincident(g2,g3)
    c: Coincident(g3,g4)
    c: Coincident(g4,g1)
    c: Horizontal(g1)
    c: Horizontal(g3)
    c: Vertical(g2)
    c: Vertical(g4)
    c: Coincident(g1,g-4)
    c: PointOnObject(g2,g-3)
    c: Symmetric(g3,g-3,g5)
    c: Symmetric(g2,g6,g5)
    c: DistanceX(g2,g6) = 226.9  'TravelDistance'
    c: PointOnObject(g7,g0)
    c: PointOnObject(g7,g-5)
    c: Vertical(g7,g0)
    c: Coincident(g8,g3)
    c: PointOnObject(g8,g-3)
    c: DistanceX(g8,g8) = 5  'EndStopToActiveDistance'
    c: PointOnObject(g9,g-4)
    c: Coincident(g9,g3)
    c: PointOnObject(g10,g-4)
    c: DistanceX(g9,g10) = 200  'MagnetoPotActiveLength'
    c: PointOnObject(g11,g-3)
    c: DistanceX(g11,g6) = 28.9
    c: Symmetric(g10,g9,g12)
    c: Symmetric(g14,g13,g12)
    c: DistanceX(g13,g14) = 215.86  'MagnetoPotPartLength'
    c: Vertical(g9,g8)
    c: Coincident(g15,g9)
    c: Vertical(g15)
    c: Coincident(g16,g15)
    c: Horizontal(g16)
    c: Coincident(g17,g16)
    c: Coincident(g18,g4)
    c: Coincident(g19,g17)
    c: Vertical(g17)
    c: DistanceY(g17,g17) = 20.3  'PartWidth'
    c: Coincident(g20,g4)
    c: Coincident(g21,g17)
    c: Coincident(g22,g4)
    c: Coincident(g22,g17)
    c: PointOnObject(g17,g1)
    c: Coincident(g17,g13)
    c: DistanceX(g14,g-4) = 28.02  'Base_End'
    c: DistanceX(g3,g3) = 14.05  'EndStopDistance'
    c: DistanceX(g4,g17) = 11.12  'Rail_To_Part'
    c: DistanceX(g16,g15) = 7.93  'PartStartToActiveStart'
FEATURE [PartDesign::Pad] Pad
  Direction = (0,0,1)
  Length = 6
  Length2 = 10
  Profile = -> Sketch
  ReferenceAxis = -> Sketch [N_Axis]
  Reversed = true
  Type = 0
FEATURE [PartDesign::SubShapeBinder] Binder001  label="MagnetoPot_Binder"
  BindCopyOnChange = 0
  BindMode = 0
  ClaimChildren = false
  Context = -> Body [Binder001.]
  Fuse = false
  MakeFace = true
  OffsetFill = false
  OffsetIntersection = false
  OffsetJoinType = 0
  OffsetOpenResult = false
  PartialLoad = false
  Placement = pos=(5,-20.5,0) rot=(0,0,1;0rad)
  Relative = true
  Support = -> [<external MagnetoPot/MagnetoPot.FCStd>#Body]
  _Version = 2
FEATURE [Sketcher::SketchObject] Sketch001
  ExternalGeometry = -> [Pad]
  FullyConstrained = true
  MapMode = 5
  Placement = pos=(0,0,-6) rot=(1,0,0;3.14159rad)
  Support = -> [Pad]
  expr: .Constraints.MagnetoPotTailWidth = 10.16
  expr: Constraints[22] = .Constraints.Strength
  expr: Constraints[23] = .Constraints.Strength
  expr: Constraints[25] = .Constraints.Strength
  expr: Constraints[28] = .Constraints.Strength
  sketch-geometry (21):
    g0: LineSegment StartX=19.05 StartY=20.3 StartZ=0 EndX=19.05 EndY=22.3 EndZ=0
    g1: LineSegment StartX=19.05 StartY=22.3 StartZ=0 EndX=9.12 EndY=22.3 EndZ=0
    g2: LineSegment StartX=9.12 StartY=22.3 StartZ=0 EndX=9.12 EndY=2 EndZ=0
    g3: LineSegment StartX=9.12 StartY=2 StartZ=0 EndX=-2 EndY=2 EndZ=0
    g4: LineSegment StartX=-2 StartY=2 StartZ=0 EndX=-2 EndY=-11 EndZ=0
    g5: LineSegment StartX=-2 StartY=-11 StartZ=0 EndX=14.05 EndY=-11 EndZ=0
    g6: LineSegment StartX=14.05 StartY=-11 StartZ=0 EndX=14.05 EndY=-9 EndZ=0
    g7: LineSegment StartX=14.05 StartY=-9 StartZ=0 EndX=0 EndY=-9 EndZ=0
    g8: LineSegment StartX=0 StartY=0 StartZ=0 EndX=0 EndY=-9 EndZ=0
    g9: LineSegment StartX=0 StartY=0 StartZ=0 EndX=11.12 EndY=0 EndZ=0
    g10: LineSegment StartX=11.12 StartY=0 StartZ=0 EndX=11.12 EndY=20.3 EndZ=0
    g11: LineSegment StartX=11.12 StartY=20.3 StartZ=0 EndX=19.05 EndY=20.3 EndZ=0
    g12: GeomPoint X=11.12 Y=15.23 Z=0
    g13: GeomPoint X=11.12 Y=10.15 Z=0
    g14: GeomPoint X=11.12 Y=5.07 Z=0
    g15: LineSegment StartX=11.12 StartY=20.3 StartZ=0 EndX=11.12 EndY=15.23 EndZ=0
    g16: LineSegment StartX=11.12 StartY=15.23 StartZ=0 EndX=9.12 EndY=15.23 EndZ=0
    g17: LineSegment StartX=9.12 StartY=15.23 StartZ=0 EndX=9.12 EndY=22.3 EndZ=0
    g18: LineSegment StartX=11.12 StartY=5.07 StartZ=0 EndX=9.12 EndY=5.07 EndZ=0
    g19: LineSegment StartX=9.12 StartY=5.07 StartZ=0 EndX=9.12 EndY=2 EndZ=0
    g20: LineSegment StartX=11.12 StartY=0 StartZ=0 EndX=11.12 EndY=5.07 EndZ=0
  constraints (48):
    c: Coincident(g0,g-7)
    c: Vertical(g0)
    c: Horizontal(g1)
    c: Coincident(g2,g1)
    c: Coincident(g3,g2)
    c: Horizontal(g3)
    c: Coincident(g4,g3)
    c: Coincident(g5,g4)
    c: Coincident(g6,g5)
    c: Coincident(g6,g-5)
    c: Coincident(g7,g6)
    c: Coincident(g7,g-5)
    c: Coincident(g8,g-4)
    c: Coincident(g8,g7)
    c: Coincident(g9,g8)
    c: Coincident(g9,g-6)
    c: Coincident(g10,g9)
    c: Coincident(g10,g-7)
    c: Coincident(g11,g10)
    c: Coincident(g11,g0)
    c: Coincident(g0,g1)
    c: DistanceY(g0,g0) = 2  'Strength'
    c: DistanceX(g1,g10) = 2
    c: DistanceY(g9,g2) = 2
    c: Vertical(g2)
    c: DistanceX(g3,g8) = 2
    c: Vertical(g4)
    c: Horizontal(g5)
    c: DistanceY(g4,g7) = 2
    c: Vertical(g6)
    c: PointOnObject(g12,g10)
    c: Symmetric(g9,g11,g13)
    c: Symmetric(g12,g14,g13)
    c: DistanceY(g14,g12) = 10.16  'MagnetoPotTailWidth'
    c: Coincident(g15,g11)
    c: Coincident(g15,g12)
    c: Coincident(g16,g12)
    c: PointOnObject(g16,g2)
    c: Horizontal(g16)
    c: Coincident(g17,g16)
    c: Coincident(g17,g1)
    c: Coincident(g18,g14)
    c: PointOnObject(g18,g2)
    c: Coincident(g19,g18)
    c: Coincident(g19,g3)
    c: Coincident(g20,g9)
    c: Coincident(g20,g18)
    c: Horizontal(g18)
FEATURE [PartDesign::Pad] Pad001
  BaseFeature = -> Pad
  Direction = (0,0,-1)
  Length = 11.5
  Length2 = 10
  Profile = -> Sketch001
  ReferenceAxis = -> Sketch001 [N_Axis]
  Reversed = true
  Type = 0
FEATURE [Sketcher::SketchObject] Sketch002
  ExternalGeometry = -> [Pad001]
  FullyConstrained = true
  MapMode = 5
  Support = -> [Pad001]
  sketch-geometry (4):
    g0: LineSegment StartX=19.05 StartY=0 StartZ=0 EndX=11.12 EndY=0 EndZ=0
    g1: LineSegment StartX=11.12 StartY=0 StartZ=0 EndX=11.12 EndY=-20.3 EndZ=0
    g2: LineSegment StartX=11.12 StartY=-20.3 StartZ=0 EndX=19.05 EndY=-20.3 EndZ=0
    g3: LineSegment StartX=19.05 StartY=-20.3 StartZ=0 EndX=19.05 EndY=0 EndZ=0
  constraints (10):
    c: Coincident(g0,g1)
    c: Coincident(g1,g2)
    c: Coincident(g2,g3)
    c: Coincident(g3,g0)
    c: Horizontal(g0)
    c: Horizontal(g2)
    c: Vertical(g1)
    c: Coincident(g0,g-4)
    c: PointOnObject(g-3,g1)
    c: Coincident(g2,g-4)
FEATURE [PartDesign::Pocket] Pocket
  BaseFeature = -> Pad001
  Direction = (0,0,-1)
  Length = 2
  Length2 = 5
  Profile = -> Sketch002
  ReferenceAxis = -> Sketch002 [N_Axis]
  Type = 0
  expr: Length = 3.5 mm - <<Datasheet>>#<<mgn9c>>.Dim_H1 + 0.5 mm
FEATURE [Sketcher::SketchObject] Sketch003
  ExternalGeometry = -> [Pocket]
  FullyConstrained = true
  MapMode = 5
  Placement = pos=(0,0,-6) rot=(1,0,0;3.14159rad)
  Support = -> [Pocket]
  expr: Constraints[1] = <<Datasheet>>#<<mgn9c>>.Dim_D
  sketch-geometry (1):
    g0: Circle CenterX=7.5 CenterY=-4.5 CenterZ=0 NormalX=0 NormalY=0 NormalZ=1 AngleXU=0 Radius=3
  constraints (2):
    c: Coincident(g0,g-3)
    c: Diameter(g0) = 6
FEATURE [PartDesign::Pocket] Pocket001
  BaseFeature = -> Pocket
  Direction = (0,0,1)
  Length = 4
  Length2 = 5
  Profile = -> Sketch003
  ReferenceAxis = -> Sketch003 [N_Axis]
  Type = 0
  expr: Length = <<Pad>>.Length - (<<Datasheet>>#<<mgn9c>>.Dim_Hr - <<Datasheet>>#<<mgn9c>>.Dim_h - 1 mm)
FEATURE [Sketcher::SketchObject] Sketch004
  FullyConstrained = true
  MapMode = 5
  Support = -> [XY_Plane001]
  expr: Constraints[10] = <<mgn9c_13>>#<<Sketch>>.Constraints.Rail_Length
  expr: Constraints[28] = <<Sketch>>.Constraints.MagnetoPotActiveLength
  expr: Constraints[29] = <<Sketch>>.Constraints.MagnetoPotPartLength
  expr: Constraints[34] = <<Sketch>>.Constraints.TravelDistance
  expr: Constraints[35] = <<Sketch>>.Constraints.EndStopDistance
  expr: Constraints[37] = <<Sketch>>.Constraints.EndStopToActiveDistance
  expr: Constraints[38] = <<Sketch>>.Constraints.PartWidth
  expr: Constraints[44] = <<Datasheet>>#<<mgn9c>>.Dim_d
  expr: Constraints[45] = <<Datasheet>>#<<mgn9c>>.Dim_E
  expr: Constraints[9] = <<Datasheet>>#<<mgn9c>>.Dim_Wr
  sketch-geometry (21):
    g0: LineSegment StartX=-255 StartY=9 StartZ=0 EndX=0 EndY=9 EndZ=0
    g1: LineSegment StartX=0 StartY=9 StartZ=0 EndX=0 EndY=0 EndZ=0
    g2: LineSegment StartX=0 StartY=0 StartZ=0 EndX=-255 EndY=0 EndZ=0
    g3: LineSegment StartX=-255 StartY=0 StartZ=0 EndX=-255 EndY=9 EndZ=0
    g4: LineSegment StartX=-35.95 StartY=-20.3 StartZ=0 EndX=-35.95 EndY=9 EndZ=0
    g5: LineSegment StartX=-35.95 StartY=9 StartZ=0 EndX=0 EndY=9 EndZ=0
    g6: LineSegment StartX=0 StartY=9 StartZ=0 EndX=0 EndY=0 EndZ=0
    g7: LineSegment StartX=0 StartY=0 StartZ=0 EndX=-28.02 EndY=0 EndZ=0
    g8: LineSegment StartX=-28.02 StartY=0 StartZ=0 EndX=-28.02 EndY=-20.3 EndZ=0
    g9: LineSegment StartX=-35.95 StartY=-20.3 StartZ=0 EndX=-28.02 EndY=-20.3 EndZ=0
    g10: GeomPoint X=-135.95 Y=0 Z=0
    g11: GeomPoint X=-235.95 Y=0 Z=0
    g12: GeomPoint X=-35.95 Y=0 Z=0
    g13: GeomPoint X=-243.88 Y=0 Z=0
    g14: GeomPoint X=-28.02 Y=0 Z=0
    g15: GeomPoint X=-240.95 Y=9 Z=0
    g16: GeomPoint X=-14.05 Y=9 Z=0
    g17: GeomPoint X=-127.5 Y=9 Z=0
    g18: Circle CenterX=-7.5 CenterY=4.5 CenterZ=0 NormalX=0 NormalY=0 NormalZ=1 AngleXU=0 Radius=1.75
    g19: GeomPoint X=-7.5 Y=4.5 Z=0
    g20: LineSegment StartX=-7.5 StartY=4.5 StartZ=0 EndX=0 EndY=4.5 EndZ=0
  constraints (46):
    c: Coincident(g0,g1)
    c: Coincident(g1,g2)
    c: Coincident(g2,g3)
    c: Coincident(g3,g0)
    c: Horizontal(g0)
    c: Horizontal(g2)
    c: Vertical(g1)
    c: Vertical(g3)
    c: Coincident(g1,g-1)
    c: DistanceY(g1,g1) = 9
    c: DistanceX(g0,g0) = 255
    c: Coincident(g4,g5)
    c: Coincident(g5,g6)
    c: Horizontal(g5)
    c: Vertical(g4)
    c: Vertical(g6)
    c: PointOnObject(g4,g0)
    c: Coincident(g7,g6)
    c: PointOnObject(g7,g2)
    c: Coincident(g8,g7)
    c: Vertical(g8)
    c: Coincident(g9,g4)
    c: Coincident(g9,g8)
    c: Horizontal(g9)
    c: PointOnObject(g10,g2)
    c: PointOnObject(g11,g2)
    c: Symmetric(g14,g13,g10)
    c: Symmetric(g11,g12,g10)
    c: DistanceX(g11,g12) = 200
    c: DistanceX(g13,g14) = 215.86
    c: Coincident(g14,g7)
    c: PointOnObject(g15,g0)
    c: PointOnObject(g16,g0)
    c: Symmetric(g15,g16,g17)
    c: DistanceX(g15,g16) = 226.9
    c: DistanceX(g0,g15) = 14.05
    c: PointOnObject(g12,g4)
    c: DistanceX(g15,g11) = 5
    c: DistanceY(g8,g8) = 20.3
    c: Coincident(g6,g1)
    c: Coincident(g19,g18)
    c: Horizontal(g20)
    c: Coincident(g18,g20)
    c: Symmetric(g5,g6,g20)
    c: Diameter(g18) = 3.5
    c: DistanceX(g18,g20) = 7.5
FEATURE [PartDesign::Pad] Pad002
  Direction = (0,0,1)
  Length = 6
  Length2 = 10
  Profile = -> Sketch004
  ReferenceAxis = -> Sketch004 [N_Axis]
  Reversed = true
  Type = 0
  expr: Length = <<Pad>>.Length
FEATURE [Sketcher::SketchObject] Sketch006
  ExternalGeometry = -> [Pad002]
  FullyConstrained = true
  MapMode = 5
  Placement = pos=(0,0,-6) rot=(1,0,0;3.14159rad)
  Support = -> [Pad002]
  expr: Constraints[18] = <<Sketch001>>.Constraints.Strength
  expr: Constraints[19] = <<Sketch001>>.Constraints.Strength
  expr: Constraints[20] = <<Sketch001>>.Constraints.Strength
  expr: Constraints[21] = <<Sketch001>>.Constraints.Strength
  expr: Constraints[23] = <<Sketch001>>.Constraints.Strength
  expr: Constraints[27] = <<Sketch001>>.Constraints.MagnetoPotTailWidth
  sketch-geometry (17):
    g0: LineSegment StartX=2 StartY=2 StartZ=0 EndX=2 EndY=-11 EndZ=0
    g1: LineSegment StartX=2 StartY=-11 StartZ=0 EndX=-35.95 EndY=-11 EndZ=0
    g2: LineSegment StartX=-35.95 StartY=-11 StartZ=0 EndX=-35.95 EndY=-9 EndZ=0
    g3: LineSegment StartX=-35.95 StartY=22.3 StartZ=0 EndX=-26.02 EndY=22.3 EndZ=0
    g4: LineSegment StartX=-26.02 StartY=22.3 StartZ=0 EndX=-26.02 EndY=15.23 EndZ=0
    g5: LineSegment StartX=-26.02 StartY=15.23 StartZ=0 EndX=-28.02 EndY=15.23 EndZ=0
    g6: LineSegment StartX=-28.02 StartY=5.07 StartZ=0 EndX=-26.02 EndY=5.07 EndZ=0
    g7: LineSegment StartX=-26.02 StartY=5.07 StartZ=0 EndX=-26.02 EndY=2 EndZ=0
    g8: LineSegment StartX=-26.02 StartY=2 StartZ=0 EndX=2 EndY=2 EndZ=0
    g9: LineSegment StartX=-35.95 StartY=22.3 StartZ=0 EndX=-35.95 EndY=20.3 EndZ=0
    g10: GeomPoint X=-28.02 Y=10.15 Z=0
    g11: LineSegment StartX=-35.95 StartY=20.3 StartZ=0 EndX=-28.02 EndY=20.3 EndZ=0
    g12: LineSegment StartX=-28.02 StartY=20.3 StartZ=0 EndX=-28.02 EndY=15.23 EndZ=0
    g13: LineSegment StartX=-28.02 StartY=5.07 StartZ=0 EndX=-28.02 EndY=0 EndZ=0
    g14: LineSegment StartX=-28.02 StartY=0 StartZ=0 EndX=0 EndY=0 EndZ=0
    g15: LineSegment StartX=0 StartY=0 StartZ=0 EndX=0 EndY=-9 EndZ=0
    g16: LineSegment StartX=0 StartY=-9 StartZ=0 EndX=-35.95 EndY=-9 EndZ=0
  constraints (42):
    c: Vertical(g0)
    c: Coincident(g1,g0)
    c: Horizontal(g1)
    c: Coincident(g2,g1)
    c: Coincident(g2,g-6)
    c: Vertical(g2)
    c: Horizontal(g3)
    c: Coincident(g4,g3)
    c: Vertical(g4)
    c: PointOnObject(g5,g-3)
    c: Horizontal(g5)
    c: Coincident(g8,g7)
    c: Coincident(g8,g0)
    c: Horizontal(g8)
    c: Coincident(g4,g5)
    c: Coincident(g6,g7)
    c: Horizontal(g6)
    c: Vertical(g7)
    c: DistanceY(g2,g2) = 2
    c: DistanceX(g-6,g0) = 2
    c: DistanceY(g-1,g0) = 2
    c: DistanceX(g-3,g7) = 2
    c: Vertical(g4,g6)
    c: DistanceY(g-5,g3) = 2
    c: Coincident(g9,g3)
    c: Vertical(g9)
    c: Coincident(g9,g-5)
    c: DistanceY(g6,g4) = 10.16
    c: Symmetric(g-5,g-3,g10)
    c: Symmetric(g5,g6,g10)
    c: Coincident(g11,g9)
    c: Coincident(g11,g-5)
    c: Coincident(g12,g11)
    c: Coincident(g12,g5)
    c: Coincident(g6,g13)
    c: Coincident(g13,g-3)
    c: Coincident(g13,g14)
    c: Coincident(g14,g-1)
    c: Coincident(g14,g15)
    c: Coincident(g15,g-6)
    c: Coincident(g15,g16)
    c: Coincident(g16,g2)
FEATURE [Sketcher::SketchObject] Sketch007  label="Measurements"
  ExternalGeometry = -> [Pocket001]
  FullyConstrained = true
  MapMode = 5
  Placement = pos=(0,0,0) rot=(1,0,0;1.5708rad)
  Support = -> [XZ_Plane]
  constraints (3):
    c: DistanceY(g-4,g-5) = 6  'BaseHeight'
    c: DistanceY(g-4,g-6) = 4  'MagnetoPotHeight'
    c: DistanceY(g-4,g-3) = 11.5  'TotalHeight'
FEATURE [PartDesign::Body] Body  label="BaseMagentoPot"
  Group = -> [Sketch,Binder,Pad,Binder001,Sketch001,Pad001,Sketch002,Pocket,Sketch003,Pocket001,Sketch007]
  Origin = -> Origin
  Tip = -> Pocket001
FEATURE [PartDesign::Pad] Pad003
  BaseFeature = -> Pad002
  Direction = (0,0,-1)
  Length = 11.5
  Length2 = 10
  Profile = -> Sketch006
  ReferenceAxis = -> Sketch006 [N_Axis]
  Reversed = true
  Type = 0
  expr: Length = Sketch007.Constraints.TotalHeight
FEATURE [Sketcher::SketchObject] Sketch008
  ExternalGeometry = -> [Pad003]
  FullyConstrained = true
  MapMode = 5
  Support = -> [Pad003]
  sketch-geometry (4):
    g0: LineSegment StartX=-35.95 StartY=-20.3 StartZ=0 EndX=-28.02 EndY=-20.3 EndZ=0
    g1: LineSegment StartX=-28.02 StartY=-20.3 StartZ=0 EndX=-28.02 EndY=0 EndZ=0
    g2: LineSegment StartX=-28.02 StartY=0 StartZ=0 EndX=-35.95 EndY=0 EndZ=0
    g3: LineSegment StartX=-35.95 StartY=0 StartZ=0 EndX=-35.95 EndY=-20.3 EndZ=0
  constraints (10):
    c: Coincident(g0,g1)
    c: Coincident(g1,g2)
    c: Coincident(g2,g3)
    c: Coincident(g3,g0)
    c: Horizontal(g0)
    c: Horizontal(g2)
    c: Vertical(g1)
    c: Vertical(g3)
    c: Coincident(g0,g-4)
    c: Coincident(g1,g-3)
FEATURE [PartDesign::Pocket] Pocket002
  BaseFeature = -> Pad003
  Direction = (0,0,-1)
  Length = 2
  Length2 = 5
  Profile = -> Sketch008
  ReferenceAxis = -> Sketch008 [N_Axis]
  Type = 0
  expr: Length = <<Measurements>>.Constraints.BaseHeight - <<Measurements>>.Constraints.MagnetoPotHeight
FEATURE [Sketcher::SketchObject] Sketch009
  ExternalGeometry = -> [Pocket002]
  FullyConstrained = true
  MapMode = 5
  Placement = pos=(0,0,5.5) rot=(0,0,1;0rad)
  Support = -> [Pocket002]
  expr: Constraints[10] = <<Sketch>>.Constraints.EndStopDistance
  expr: Constraints[11] = <<Datasheet>>#<<mgn9c>>.Dim_W
  sketch-geometry (5):
    g0: LineSegment StartX=-35.95 StartY=14.5 StartZ=0 EndX=-14.05 EndY=14.5 EndZ=0
    g1: LineSegment StartX=-14.05 StartY=14.5 StartZ=0 EndX=-14.05 EndY=-5.5 EndZ=0
    g2: LineSegment StartX=-14.05 StartY=-5.5 StartZ=0 EndX=-35.95 EndY=-5.5 EndZ=0
    g3: LineSegment StartX=-35.95 StartY=-5.5 StartZ=0 EndX=-35.95 EndY=14.5 EndZ=0
    g4: LineSegment StartX=-7.5 StartY=4.5 StartZ=0 EndX=-35.95 EndY=4.5 EndZ=0
  constraints (14):
    c: Coincident(g0,g1)
    c: Coincident(g1,g2)
    c: Coincident(g2,g3)
    c: Coincident(g3,g0)
    c: Horizontal(g0)
    c: Horizontal(g2)
    c: Vertical(g1)
    c: Vertical(g3)
    c: Coincident(g4,g-5)
    c: PointOnObject(g4,g3)
    c: DistanceX(g0,g-6) = 14.05
    c: DistanceY(g3,g3) = 20
    c: Symmetric(g0,g2,g4)
    c: PointOnObject(g-6,g3)
FEATURE [PartDesign::Pocket] Pocket003
  BaseFeature = -> Pocket002
  Direction = (0,0,-1)
  Length = 5
  Length2 = 5
  Profile = -> Sketch009
  ReferenceAxis = -> Sketch009 [N_Axis]
  Type = 2
FEATURE [Sketcher::SketchObject] Sketch010
  ExternalGeometry = -> [Pocket003]
  FullyConstrained = true
  MapMode = 5
  Placement = pos=(0,0,-6) rot=(1,0,0;3.14159rad)
  Support = -> [Pocket003]
  expr: Constraints[1] = <<Datasheet>>#<<mgn9c>>.Dim_D
  sketch-geometry (1):
    g0: Circle CenterX=-7.5 CenterY=-4.5 CenterZ=0 NormalX=0 NormalY=0 NormalZ=1 AngleXU=0 Radius=3
  constraints (2):
    c: Coincident(g0,g-3)
    c: Diameter(g0) = 6
FEATURE [PartDesign::Pocket] Pocket004
  BaseFeature = -> Pocket003
  Direction = (0,0,1)
  Length = 4
  Length2 = 5
  Profile = -> Sketch010
  ReferenceAxis = -> Sketch010 [N_Axis]
  Type = 0
  expr: Length = <<Pad002>>.Length - (<<Datasheet>>#<<mgn9c>>.Dim_Hr - <<Datasheet>>#<<mgn9c>>.Dim_h - 1 mm)
FEATURE [PartDesign::Body] Body001  label="BaseMagnetoPot_Opposite"
  Group = -> [Sketch004,Pad002,Sketch006,Pad003,Sketch008,Pocket002,Sketch009,Pocket003,Sketch010,Pocket004]
  Origin = -> Origin001
  Placement = pos=(-11,0,0) rot=(0,0,1;0rad)
  Tip = -> Pocket004
---- part parts/MG/mgn9c_13.FCStd = doc fcstd_af4c73f2d28f ----
FCSTD DOCUMENT  (FreeCAD 0.21R33668 +26 (Git))
Label: mgn9c_13
License: All rights reserved
LicenseURL: http://en.wikipedia.org/wiki/All_rights_reserved
objects: Sketcher::SketchObject×2, App::Link×1, PartDesign::Pad×1, PartDesign::Pocket×1, PartDesign::LinearPattern×1, PartDesign::Body×1
note: 8 computed .brp shape members not serialized (recipe doc carries the construction recipe); baked Part::Feature solids carry a one-line shape summary decoded from their .brp
EXTERNAL_REF file=Datasheet.FCStd obj=Spreadsheet

FEATURE [App::Link] Link  label="mgn9c"
  LinkedObject = -> <external Datasheet.FCStd>#Spreadsheet
FEATURE [Sketcher::SketchObject] Sketch
  Base_Number_Holes = 13
  FullyConstrained = true
  MapMode = 5
  Support = -> [XY_Plane]
  expr: Constraints[10] = <<mgn9c>>.Dim_Wr
  sketch-geometry (4):
    g0: LineSegment StartX=0 StartY=0 StartZ=0 EndX=255 EndY=0 EndZ=0
    g1: LineSegment StartX=255 StartY=0 StartZ=0 EndX=255 EndY=9 EndZ=0
    g2: LineSegment StartX=255 StartY=9 StartZ=0 EndX=0 EndY=9 EndZ=0
    g3: LineSegment StartX=0 StartY=9 StartZ=0 EndX=0 EndY=0 EndZ=0
  constraints (11):
    c: Coincident(g0,g1)
    c: Coincident(g1,g2)
    c: Coincident(g2,g3)
    c: Coincident(g3,g0)
    c: Horizontal(g0)
    c: Horizontal(g2)
    c: Vertical(g1)
    c: Vertical(g3)
    c: Coincident(g0,g-1)
    c: DistanceX(g2,g2) = 255  'Rail_Length'
    c: DistanceY(g3,g3) = 9
FEATURE [PartDesign::Pad] Pad
  Direction = (0,0,1)
  Length = 6.5
  Length2 = 10
  Profile = -> Sketch
  ReferenceAxis = -> Sketch [N_Axis]
  Type = 0
  expr: Length = <<mgn9c>>.Dim_Hr
FEATURE [Sketcher::SketchObject] Sketch001
  FullyConstrained = true
  MapMode = 5
  Placement = pos=(0,0,6.5) rot=(0,0,1;0rad)
  Support = -> [Pad]
  expr: Constraints[0] = <<mgn9c>>.Dim_E
  expr: Constraints[1] = <<mgn9c>>.Dim_Wr / 2
  expr: Constraints[2] = <<mgn9c>>.Dim_d
  sketch-geometry (1):
    g0: Circle CenterX=7.5 CenterY=4.5 CenterZ=0 NormalX=0 NormalY=0 NormalZ=1 AngleXU=0 Radius=1.75
  constraints (3):
    c: DistanceX(g-1,g0) = 7.5
    c: DistanceY(g-1,g0) = 4.5
    c: Diameter(g0) = 3.5
FEATURE [PartDesign::Pocket] Pocket
  BaseFeature = -> Pad
  Direction = (0,0,-1)
  Length = 6.5
  Length2 = 5
  Profile = -> Sketch001
  ReferenceAxis = -> Sketch001 [N_Axis]
  Type = 0
  expr: Length = <<mgn9c>>.Dim_Hr
FEATURE [PartDesign::LinearPattern] LinearPattern
  BaseFeature = -> Pocket
  Direction = -> Sketch001 [H_Axis]
  Length = 240
  Occurrences = 13
  Originals = -> [Pocket]
  expr: Length = <<Sketch>>.Constraints.Rail_Length - <<mgn9c>>.Dim_E * 2
  expr: Occurrences = <<Sketch>>.Base_Number_Holes
FEATURE [PartDesign::Body] Body  label="Rail"
  Group = -> [Sketch,Pad,Sketch001,Pocket,LinearPattern]
  Origin = -> Origin
  Tip = -> LinearPattern
---- part parts/MG/mgn9c_slide.FCStd = doc fcstd_17b450fab925 ----
FCSTD DOCUMENT  (FreeCAD 0.21R33668 +26 (Git))
Label: mgn9c_slide
License: All rights reserved
LicenseURL: http://en.wikipedia.org/wiki/All_rights_reserved
objects: Sketcher::SketchObject×4, PartDesign::Pocket×3, App::Link×1, PartDesign::Pad×1, PartDesign::Body×1
note: 13 computed .brp shape members not serialized (recipe doc carries the construction recipe); baked Part::Feature solids carry a one-line shape summary decoded from their .brp
EXTERNAL_REF file=Datasheet.FCStd obj=Spreadsheet

FEATURE [App::Link] Link  label="mgn9c"
  LinkedObject = -> <external Datasheet.FCStd>#Spreadsheet
FEATURE [Sketcher::SketchObject] Sketch002
  FullyConstrained = true
  MapMode = 5
  Support = -> [XY_Plane001]
  expr: Constraints[10] = <<mgn9c>>.Dim_W
  expr: Constraints[9] = <<mgn9c>>.Dim_L
  sketch-geometry (4):
    g0: LineSegment StartX=0 StartY=0 StartZ=0 EndX=28.9 EndY=0 EndZ=0
    g1: LineSegment StartX=28.9 StartY=0 StartZ=0 EndX=28.9 EndY=20 EndZ=0
    g2: LineSegment StartX=28.9 StartY=20 StartZ=0 EndX=0 EndY=20 EndZ=0
    g3: LineSegment StartX=0 StartY=20 StartZ=0 EndX=0 EndY=0 EndZ=0
  constraints (11):
    c: Coincident(g0,g1)
    c: Coincident(g1,g2)
    c: Coincident(g2,g3)
    c: Coincident(g3,g0)
    c: Horizontal(g0)
    c: Horizontal(g2)
    c: Vertical(g1)
    c: Vertical(g3)
    c: Coincident(g0,g-1)
    c: DistanceX(g2,g2) = 28.9
    c: DistanceY(g1,g1) = 20
FEATURE [PartDesign::Pad] Pad001
  Direction = (0,0,1)
  Length = 8
  Length2 = 10
  Profile = -> Sketch002
  ReferenceAxis = -> Sketch002 [N_Axis]
  Type = 0
  expr: Length = <<mgn9c>>.Dim_H - <<mgn9c>>.Dim_H1
FEATURE [Sketcher::SketchObject] Sketch003
  ExternalGeometry = -> [Pad001]
  FullyConstrained = true
  MapMode = 5
  Placement = pos=(0,0,0) rot=(0.57735,-0.57735,-0.57735;2.0944rad)
  Support = -> [Pad001]
  expr: Constraints[10] = <<mgn9c>>.Dim_Hr - <<mgn9c>>.Dim_H1
  expr: Constraints[8] = <<mgn9c>>.Dim_N
  expr: Constraints[9] = <<mgn9c>>.Dim_N
  sketch-geometry (4):
    g0: LineSegment StartX=-14.5 StartY=0 StartZ=0 EndX=-5.5 EndY=0 EndZ=0
    g1: LineSegment StartX=-5.5 StartY=0 StartZ=0 EndX=-5.5 EndY=4.5 EndZ=0
    g2: LineSegment StartX=-5.5 StartY=4.5 StartZ=0 EndX=-14.5 EndY=4.5 EndZ=0
    g3: LineSegment StartX=-14.5 StartY=4.5 StartZ=0 EndX=-14.5 EndY=0 EndZ=0
  constraints (12):
    c: Coincident(g0,g1)
    c: Coincident(g1,g2)
    c: Coincident(g2,g3)
    c: Coincident(g3,g0)
    c: Horizontal(g0)
    c: Horizontal(g2)
    c: Vertical(g1)
    c: Vertical(g3)
    c: DistanceX(g-5,g0) = 5.5
    c: DistanceX(g0,g-6) = 5.5
    c: DistanceY(g1,g1) = 4.5
    c: PointOnObject(g0,g-5)
FEATURE [PartDesign::Pocket] Pocket001
  BaseFeature = -> Pad001
  Direction = (1,0,0)
  Length = 28.9
  Length2 = 5
  Profile = -> Sketch003
  ReferenceAxis = -> Sketch003 [N_Axis]
  Type = 0
  expr: Length = <<mgn9c>>.Dim_L
FEATURE [Sketcher::SketchObject] Sketch004
  ExternalGeometry = -> [Pocket001]
  FullyConstrained = true
  MapMode = 5
  Placement = pos=(0,0,8) rot=(0,0,1;0rad)
  Support = -> [Pocket001]
  expr: Constraints[17] = 3
  expr: Constraints[18] = 3
  expr: Constraints[19] = 3
  expr: Constraints[20] = 3
  expr: Constraints[8] = <<mgn9c>>.Dim_C
  expr: Constraints[9] = <<mgn9c>>.Dim_B
  sketch-geometry (9):
    g0: LineSegment StartX=9.45 StartY=17.5 StartZ=0 EndX=19.45 EndY=17.5 EndZ=0
    g1: LineSegment StartX=19.45 StartY=17.5 StartZ=0 EndX=19.45 EndY=2.5 EndZ=0
    g2: LineSegment StartX=19.45 StartY=2.5 StartZ=0 EndX=9.45 EndY=2.5 EndZ=0
    g3: LineSegment StartX=9.45 StartY=2.5 StartZ=0 EndX=9.45 EndY=17.5 EndZ=0
    g4: GeomPoint X=14.45 Y=10 Z=0
    g5: Circle CenterX=9.45 CenterY=17.5 CenterZ=0 NormalX=0 NormalY=0 NormalZ=1 AngleXU=0 Radius=1.5
    g6: Circle CenterX=19.45 CenterY=17.5 CenterZ=0 NormalX=0 NormalY=0 NormalZ=1 AngleXU=0 Radius=1.5
    g7: Circle CenterX=19.45 CenterY=2.5 CenterZ=0 NormalX=0 NormalY=0 NormalZ=1 AngleXU=0 Radius=1.5
    g8: Circle CenterX=9.45 CenterY=2.5 CenterZ=0 NormalX=0 NormalY=0 NormalZ=1 AngleXU=0 Radius=1.5
  constraints (21):
    c: Coincident(g0,g1)
    c: Coincident(g1,g2)
    c: Coincident(g2,g3)
    c: Coincident(g3,g0)
    c: Horizontal(g0)
    c: Horizontal(g2)
    c: Vertical(g1)
    c: Vertical(g3)
    c: DistanceX(g0,g0) = 10
    c: DistanceY(g1,g1) = 15
    c: DistanceY(g-4,g2) = 2.5
    c: Symmetric(g-3,g-4,g4)
    c: Symmetric(g1,g0,g4)
    c: Coincident(g5,g0)
    c: Coincident(g6,g0)
    c: Coincident(g7,g1)
    c: Coincident(g8,g2)
    c: Diameter(g8) = 3
    c: Diameter(g7) = 3
    c: Diameter(g6) = 3
    c: Diameter(g5) = 3
FEATURE [PartDesign::Pocket] Pocket002
  BaseFeature = -> Pocket001
  Direction = (0,0,-1)
  Length = 3
  Length2 = 5
  Profile = -> Sketch004
  ReferenceAxis = -> Sketch004 [N_Axis]
  Type = 0
FEATURE [Sketcher::SketchObject] Sketch005
  ExternalGeometry = -> [Pocket002]
  FullyConstrained = true
  MapMode = 5
  Placement = pos=(0,0,8) rot=(0,0,1;0rad)
  Support = -> [Pocket002]
  expr: Constraints[19] = <<mgn9c>>.Dim_L1
  sketch-geometry (9):
    g0: LineSegment StartX=0 StartY=20 StartZ=0 EndX=5 EndY=20 EndZ=0
    g1: LineSegment StartX=5 StartY=20 StartZ=0 EndX=5 EndY=0 EndZ=0
    g2: LineSegment StartX=5 StartY=0 StartZ=0 EndX=0 EndY=0 EndZ=0
    g3: LineSegment StartX=0 StartY=0 StartZ=0 EndX=0 EndY=20 EndZ=0
    g4: LineSegment StartX=28.9 StartY=0 StartZ=0 EndX=23.9 EndY=0 EndZ=0
    g5: LineSegment StartX=23.9 StartY=0 StartZ=0 EndX=23.9 EndY=20 EndZ=0
    g6: LineSegment StartX=23.9 StartY=20 StartZ=0 EndX=28.9 EndY=20 EndZ=0
    g7: LineSegment StartX=28.9 StartY=20 StartZ=0 EndX=28.9 EndY=0 EndZ=0
    g8: GeomPoint X=14.45 Y=0 Z=0
  constraints (22):
    c: Coincident(g0,g1)
    c: Coincident(g1,g2)
    c: Coincident(g2,g3)
    c: Coincident(g3,g0)
    c: Horizontal(g0)
    c: Horizontal(g2)
    c: Vertical(g1)
    c: Vertical(g3)
    c: Coincident(g0,g-3)
    c: PointOnObject(g1,g-1)
    c: Coincident(g4,g5)
    c: Coincident(g5,g6)
    c: Coincident(g6,g7)
    c: Coincident(g7,g4)
    c: Horizontal(g6)
    c: Vertical(g5)
    c: Vertical(g7)
    c: Symmetric(g2,g-4,g8)
    c: Symmetric(g4,g1,g8)
    c: DistanceX(g1,g4) = 18.9
    c: PointOnObject(g5,g-5)
    c: Coincident(g4,g-4)
FEATURE [PartDesign::Pocket] Pocket003
  BaseFeature = -> Pocket002
  Direction = (0,0,-1)
  Length = 0.1
  Length2 = 5
  Profile = -> Sketch005
  ReferenceAxis = -> Sketch005 [N_Axis]
  Type = 0
FEATURE [PartDesign::Body] Body001  label="Slide"
  Group = -> [Sketch002,Pad001,Sketch003,Pocket001,Sketch004,Pocket002,Sketch005,Pocket003]
  Origin = -> Origin001
  Tip = -> Pocket003
---- part parts/MagnetoPot/MagnetoPot.FCStd = doc fcstd_ba503c3fc88b ----
FCSTD DOCUMENT  (FreeCAD 0.21R33668 +26 (Git))
Label: MagnetoPot
License: All rights reserved
LicenseURL: http://en.wikipedia.org/wiki/All_rights_reserved
objects: Sketcher::SketchObject×2, PartDesign::Pad×1, PartDesign::Body×1
note: 5 computed .brp shape members not serialized (recipe doc carries the construction recipe); baked Part::Feature solids carry a one-line shape summary decoded from their .brp

FEATURE [Sketcher::SketchObject] Sketch
  FullyConstrained = true
  MapMode = 5
  Support = -> [XY_Plane]
  sketch-geometry (17):
    g0: LineSegment StartX=0 StartY=0 StartZ=0 EndX=215.86 EndY=0 EndZ=0
    g1: LineSegment StartX=215.86 StartY=0 StartZ=0 EndX=215.86 EndY=20.3 EndZ=0
    g2: LineSegment StartX=215.86 StartY=20.3 StartZ=0 EndX=0 EndY=20.3 EndZ=0
    g3: LineSegment StartX=0 StartY=20.3 StartZ=0 EndX=0 EndY=0 EndZ=0
    g4: LineSegment StartX=7.93 StartY=8.245 StartZ=0 EndX=207.93 EndY=8.245 EndZ=0
    g5: LineSegment StartX=207.93 StartY=8.245 StartZ=0 EndX=207.93 EndY=12.055 EndZ=0
    g6: LineSegment StartX=207.93 StartY=12.055 StartZ=0 EndX=7.93 EndY=12.055 EndZ=0
    g7: LineSegment StartX=7.93 StartY=12.055 StartZ=0 EndX=7.93 EndY=8.245 EndZ=0
    g8: GeomPoint X=107.93 Y=10.15 Z=0
    g9: LineSegment StartX=-24.89 StartY=15.23 StartZ=0 EndX=0 EndY=15.23 EndZ=0
    g10: LineSegment StartX=0 StartY=15.23 StartZ=0 EndX=0 EndY=5.07 EndZ=0
    g11: LineSegment StartX=0 StartY=5.07 StartZ=0 EndX=-24.89 EndY=5.07 EndZ=0
    g12: LineSegment StartX=-24.89 StartY=5.07 StartZ=0 EndX=-24.89 EndY=15.23 EndZ=0
    g13: LineSegment StartX=0 StartY=20.3 StartZ=0 EndX=0 EndY=15.23 EndZ=0
    g14: LineSegment StartX=0 StartY=5.07 StartZ=0 EndX=0 EndY=0 EndZ=0
    g15: GeomPoint X=0 Y=10.15 Z=0
    g16: LineSegment StartX=215.86 StartY=20.3 StartZ=0 EndX=215.86 EndY=0 EndZ=0
  constraints (42):
    c: Coincident(g0,g1)
    c: Coincident(g1,g2)
    c: Coincident(g2,g3)
    c: Coincident(g3,g0)
    c: Horizontal(g0)
    c: Horizontal(g2)
    c: Vertical(g1)
    c: Vertical(g3)
    c: Coincident(g0,g-1)
    c: DistanceX(g2,g2) = 215.86  'PartLength'
    c: DistanceY(g3,g3) = 20.3  'PartWidth'
    c: Coincident(g4,g5)
    c: Coincident(g5,g6)
    c: Coincident(g6,g7)
    c: Coincident(g7,g4)
    c: Horizontal(g4)
    c: Horizontal(g6)
    c: Vertical(g5)
    c: Vertical(g7)
    c: Symmetric(g2,g0,g8)
    c: Symmetric(g4,g5,g8)
    c: DistanceY(g5,g5) = 3.81  'ActiveWidth'
    c: DistanceX(g6,g6) = 200  'ActiveLength'
    c: Coincident(g9,g10)
    c: Coincident(g10,g11)
    c: Coincident(g11,g12)
    c: Coincident(g12,g9)
    c: Horizontal(g9)
    c: Horizontal(g11)
    c: Vertical(g10)
    c: Vertical(g12)
    c: Coincident(g13,g2)
    c: Coincident(g13,g9)
    c: Coincident(g14,g11)
    c: Coincident(g14,g0)
    c: Symmetric(g2,g0,g15)
    c: Symmetric(g9,g11,g15)
    c: DistanceX(g9,g9) = 24.89  'TailLength'
    c: DistanceY(g12,g12) = 10.16  'TailWidth'
    c: Coincident(g16,g2)
    c: Coincident(g16,g0)
    c: DistanceY(g0,g4) = 8.245  'EdgeToActiveWidth'
FEATURE [PartDesign::Pad] Pad
  Direction = (0,0,1)
  Length = 3.5
  Length2 = 10
  Profile = -> Sketch
  ReferenceAxis = -> Sketch [N_Axis]
  Type = 0
FEATURE [Sketcher::SketchObject] Sketch001
  ExternalGeometry = -> [Pad]
  FullyConstrained = true
  MapMode = 5
  Placement = pos=(0,0,0) rot=(1,0,0;1.5708rad)
  Support = -> [Pad]
  constraints (1):
    c: DistanceY(g-1,g-3) = 3.5  'Height'
FEATURE [PartDesign::Body] Body  label="MP1_L_0200_103_5_ST"
  Group = -> [Sketch,Pad,Sketch001]
  Origin = -> Origin
  Tip = -> Pad
---- part parts/NormalConnectorWithPin.FCStd = doc fcstd_db2ac3e29eb3 ----
FCSTD DOCUMENT  (FreeCAD 0.21R33668 +26 (Git))
Label: NormalConnectorWithPin
License: All rights reserved
LicenseURL: http://en.wikipedia.org/wiki/All_rights_reserved
objects: Sketcher::SketchObject×6, PartDesign::SubShapeBinder×4, PartDesign::Pocket×4, PartDesign::Pad×2, PartDesign::Body×1
note: 23 computed .brp shape members not serialized (recipe doc carries the construction recipe); baked Part::Feature solids carry a one-line shape summary decoded from their .brp
EXTERNAL_REF file=MG/mgn9c_slide.FCStd obj=Body001
EXTERNAL_REF file=MG/mgn9c_13.FCStd obj=Body
EXTERNAL_REF file=MagnetoPot/MagnetoPot.FCStd obj=Sketch
EXTERNAL_REF file=OmniballConnector/OmniballConnector_7945.FCStd obj=Body
EXTERNAL_REF file=MagnetoPot/MagnetoPot.FCStd obj=Body
EXTERNAL_REF file=MG/Datasheet.FCStd obj=Spreadsheet
EXTERNAL_REF file=OmniballConnector/OmniballConnector_7945.FCStd obj=Sketch002
EXTERNAL_REF file=OmniballConnector/OmniballConnector_7945.FCStd obj=Sketch

FEATURE [PartDesign::SubShapeBinder] Binder  label="Slide"
  BindCopyOnChange = 0
  BindMode = 0
  ClaimChildren = false
  Context = -> Body [Binder.]
  Fuse = false
  MakeFace = true
  OffsetFill = false
  OffsetIntersection = false
  OffsetJoinType = 0
  OffsetOpenResult = false
  PartialLoad = false
  Relative = true
  Support = -> [<external MG/mgn9c_slide.FCStd>#Body001]
  _Version = 2
FEATURE [PartDesign::SubShapeBinder] Binder001  label="Rail"
  BindCopyOnChange = 0
  BindMode = 0
  ClaimChildren = false
  Context = -> Body [Binder001.]
  Fuse = false
  MakeFace = true
  OffsetFill = false
  OffsetIntersection = false
  OffsetJoinType = 0
  OffsetOpenResult = false
  PartialLoad = false
  Placement = pos=(0,5.5,-2) rot=(0,0,1;0rad)
  Relative = true
  Support = -> [<external MG/mgn9c_13.FCStd>#Body]
  _Version = 2
FEATURE [Sketcher::SketchObject] Sketch
  ExternalGeometry = -> [Binder]
  FullyConstrained = true
  MapMode = 5
  Placement = pos=(0,0,8) rot=(0,0,1;0rad)
  Support = -> [Binder]
  expr: Constraints[18] = <<MagnetoPot>>#<<Sketch>>.Constraints.PartWidth
  sketch-geometry (8):
    g0: LineSegment StartX=5 StartY=20 StartZ=0 EndX=23.9 EndY=20 EndZ=0
    g1: LineSegment StartX=23.9 StartY=20 StartZ=0 EndX=23.9 EndY=-14.8 EndZ=0
    g2: LineSegment StartX=23.9 StartY=-14.8 StartZ=0 EndX=5 EndY=-14.8 EndZ=0
    g3: LineSegment StartX=5 StartY=-14.8 StartZ=0 EndX=5 EndY=20 EndZ=0
    g4: Circle CenterX=9.45 CenterY=17.5 CenterZ=0 NormalX=0 NormalY=0 NormalZ=1 AngleXU=0 Radius=1.5
    g5: Circle CenterX=9.45 CenterY=2.5 CenterZ=0 NormalX=0 NormalY=0 NormalZ=1 AngleXU=0 Radius=1.5
    g6: Circle CenterX=19.45 CenterY=2.5 CenterZ=0 NormalX=0 NormalY=0 NormalZ=1 AngleXU=0 Radius=1.5
    g7: Circle CenterX=19.45 CenterY=17.5 CenterZ=0 NormalX=0 NormalY=0 NormalZ=1 AngleXU=0 Radius=1.5
  constraints (19):
    c: Coincident(g0,g1)
    c: Coincident(g1,g2)
    c: Coincident(g2,g3)
    c: Coincident(g3,g0)
    c: Horizontal(g0)
    c: Horizontal(g2)
    c: Vertical(g1)
    c: Vertical(g3)
    c: Coincident(g0,g-5)
    c: Coincident(g4,g-12)
    c: PointOnObject(g-11,g4)
    c: Coincident(g5,g-14)
    c: PointOnObject(g-13,g5)
    c: Coincident(g6,g-8)
    c: PointOnObject(g-7,g6)
    c: Coincident(g7,g-10)
    c: PointOnObject(g-9,g7)
    c: PointOnObject(g-6,g1)
    c: DistanceY(g1,g-15) = 20.3
FEATURE [PartDesign::Pad] Pad
  Direction = (0,0,1)
  Length = 1.5
  Length2 = 10
  Profile = -> Sketch
  ReferenceAxis = -> Sketch [N_Axis]
  Type = 0
  expr: Length = (6 - 3) / 2
FEATURE [PartDesign::SubShapeBinder] Binder002  label="Omniball"
  BindCopyOnChange = 0
  BindMode = 0
  ClaimChildren = false
  Context = -> Body [Binder002.]
  Fuse = false
  MakeFace = true
  OffsetFill = false
  OffsetIntersection = false
  OffsetJoinType = 0
  OffsetOpenResult = false
  PartialLoad = false
  Placement = pos=(11,-5,0) rot=(0,0,1;0rad)
  Relative = true
  Support = -> [<external OmniballConnector/OmniballConnector_7945.FCStd>#Body]
  _Version = 2
FEATURE [PartDesign::SubShapeBinder] Binder003  label="MagnetoPot"
  BindCopyOnChange = 0
  BindMode = 0
  ClaimChildren = false
  Context = -> Body [Binder003.]
  Fuse = false
  MakeFace = true
  OffsetFill = false
  OffsetIntersection = false
  OffsetJoinType = 0
  OffsetOpenResult = false
  PartialLoad = false
  Placement = pos=(0,-15,-4.5) rot=(0,0,1;0rad)
  Relative = true
  Support = -> [<external MagnetoPot/MagnetoPot.FCStd>#Body]
  _Version = 2
FEATURE [Sketcher::SketchObject] Sketch001
  ExternalGeometry = -> [Binder,Pad]
  FullyConstrained = true
  MapMode = 5
  Placement = pos=(0,0,8) rot=(1,0,0;3.14159rad)
  Support = -> [Pad]
  sketch-geometry (4):
    g0: LineSegment StartX=5 StartY=0 StartZ=0 EndX=23.9 EndY=0 EndZ=0
    g1: LineSegment StartX=23.9 StartY=0 StartZ=0 EndX=23.9 EndY=14.8 EndZ=0
    g2: LineSegment StartX=23.9 StartY=14.8 StartZ=0 EndX=5 EndY=14.8 EndZ=0
    g3: LineSegment StartX=5 StartY=14.8 StartZ=0 EndX=5 EndY=0 EndZ=0
  constraints (11):
    c: Coincident(g0,g1)
    c: Coincident(g1,g2)
    c: Coincident(g2,g3)
    c: Coincident(g3,g0)
    c: Horizontal(g0)
    c: Horizontal(g2)
    c: Vertical(g1)
    c: Vertical(g3)
    c: PointOnObject(g0,g-3)
    c: Coincident(g1,g-4)
    c: PointOnObject(g0,g-5)
FEATURE [PartDesign::Pad] Pad001
  BaseFeature = -> Pad
  Direction = (0,0,-1)
  Length = 8
  Length2 = 10
  Profile = -> Sketch001
  ReferenceAxis = -> Sketch001 [N_Axis]
  Type = 0
  expr: Length = <<Datasheet>>#<<mgn9c>>.Dim_H - <<Datasheet>>#<<mgn9c>>.Dim_H1
FEATURE [Sketcher::SketchObject] Sketch002  label="BusPins"
  ExternalGeometry = -> [Pad001]
  FullyConstrained = true
  MapMode = 5
  Placement = pos=(0,0,0) rot=(1,0,0;3.14159rad)
  Support = -> [Pad001]
  expr: .Constraints.Radius = <<OmniballConnector_7945>>#<<Sketch002>>.Constraints.Smallest_Radius
  expr: Constraints[1] = <<OmniballConnector_7945>>#<<Sketch002>>.Constraints.Smallest_Radius
  expr: Constraints[2] = <<OmniballConnector_7945>>#<<Sketch002>>.Constraints.Smallest_Radius
  expr: Constraints[3] = <<OmniballConnector_7945>>#<<Sketch002>>.Constraints.Smallest_Radius
  expr: Constraints[44] = .Constraints.Dist
  expr: Constraints[4] = <<OmniballConnector_7945>>#<<Sketch002>>.Constraints.Smallest_Radius
  expr: Constraints[5] = <<OmniballConnector_7945>>#<<Sketch002>>.Constraints.Smallest_Radius
  expr: Constraints[6] = <<OmniballConnector_7945>>#<<Sketch002>>.Constraints.Smallest_Radius
  sketch-geometry (22):
    g0: Circle CenterX=17.5735 CenterY=2.15 CenterZ=0 NormalX=0 NormalY=0 NormalZ=1 AngleXU=0 Radius=1.2954
    g1: Circle CenterX=20.6046 CenterY=3.9 CenterZ=0 NormalX=0 NormalY=0 NormalZ=1 AngleXU=0 Radius=1.2954
    g2: Circle CenterX=17.5735 CenterY=5.65 CenterZ=0 NormalX=0 NormalY=0 NormalZ=1 AngleXU=0 Radius=1.2954
    g3: Circle CenterX=17.5735 CenterY=9.15 CenterZ=0 NormalX=0 NormalY=0 NormalZ=1 AngleXU=0 Radius=1.2954
    g4: Circle CenterX=20.6046 CenterY=10.9 CenterZ=0 NormalX=0 NormalY=0 NormalZ=1 AngleXU=0 Radius=1.2954
    g5: Circle CenterX=20.6046 CenterY=7.4 CenterZ=0 NormalX=0 NormalY=0 NormalZ=1 AngleXU=0 Radius=1.2954
    g6: Circle CenterX=17.5735 CenterY=12.65 CenterZ=0 NormalX=0 NormalY=0 NormalZ=1 AngleXU=0 Radius=1.2954
    g7: LineSegment StartX=17.5735 StartY=12.65 StartZ=0 EndX=17.5735 EndY=2.15 EndZ=0
    g8: GeomPoint X=17.5735 Y=10.9 Z=0
    g9: GeomPoint X=17.5735 Y=7.4 Z=0
    g10: GeomPoint X=17.5735 Y=3.9 Z=0
    g11: LineSegment StartX=20.6046 StartY=10.9 StartZ=0 EndX=20.6046 EndY=3.9 EndZ=0
    g12: LineSegment StartX=17.5735 StartY=2.15 StartZ=0 EndX=20.6046 EndY=3.9 EndZ=0
    g13: LineSegment StartX=20.6046 StartY=3.9 StartZ=0 EndX=17.5735 EndY=5.65 EndZ=0
    g14: GeomPoint X=18.6954 Y=5.0023 Z=0
    g15: GeomPoint X=19.4828 Y=4.5477 Z=0
    g16: GeomPoint X=18.6954 Y=2.7977 Z=0
    g17: GeomPoint X=19.4828 Y=3.2523 Z=0
    g18: GeomPoint X=17.5735 Y=4.3546 Z=0
    g19: GeomPoint X=17.5735 Y=3.4454 Z=0
    g20: GeomPoint X=23.9 Y=7.4 Z=0
    g21: GeomPoint X=21.9 Y=7.4 Z=0
  constraints (46):
    c: Diameter(g0) = 2.5908  'Radius'
    c: Diameter(g1) = 2.5908
    c: Diameter(g2) = 2.5908
    c: Diameter(g5) = 2.5908
    c: Diameter(g4) = 2.5908
    c: Diameter(g3) = 2.5908
    c: Diameter(g6) = 2.5908
    c: Coincident(g7,g6)
    c: Coincident(g7,g0)
    c: Vertical(g7)
    c: Horizontal(g1,g10)
    c: Horizontal(g5,g9)
    c: Coincident(g11,g4)
    c: Coincident(g11,g1)
    c: Vertical(g11)
    c: Symmetric(g6,g3,g8)
    c: Symmetric(g3,g2,g9)
    c: Symmetric(g0,g2,g10)
    c: Symmetric(g4,g1,g5)
    c: Coincident(g12,g0)
    c: Coincident(g12,g1)
    c: Coincident(g13,g1)
    c: Coincident(g13,g2)
    c: PointOnObject(g14,g2)
    c: PointOnObject(g15,g1)
    c: PointOnObject(g16,g0)
    c: PointOnObject(g17,g1)
    c: PointOnObject(g17,g12)
    c: PointOnObject(g16,g12)
    c: PointOnObject(g14,g13)
    c: PointOnObject(g15,g13)
    c: PointOnObject(g18,g2)
    c: PointOnObject(g19,g0)
    c: PointOnObject(g19,g7)
    c: PointOnObject(g18,g7)
    c: Symmetric(g6,g0,g9)
    c: Symmetric(g3,g0,g2)
    c: Symmetric(g-4,g-4,g20)
    c: Horizontal(g5,g20)
    c: PointOnObject(g21,g5)
    c: Horizontal(g21,g5)
    c: DistanceY(g6,g-4) = 2.15  'BusOutsideDistance'
    c: DistanceX(g21,g20) = 2
    c: DistanceY(g0,g2) = 3.5  'Dist'
    c: Distance(g0,g1) = 3.5
    c: DistanceX(g6,g-4) = 6.32649  'ActiveStartToBusDistance'
FEATURE [PartDesign::Pocket] Pocket  label="Bus"
  BaseFeature = -> Pad001
  Direction = (0,0,1)
  Length = 5
  Length2 = 5
  Profile = -> Sketch002
  ReferenceAxis = -> Sketch002 [N_Axis]
  Type = 1
FEATURE [Sketcher::SketchObject] Sketch003
  ExternalGeometry = -> [Pocket,Binder]
  FullyConstrained = true
  MapMode = 5
  Placement = pos=(0,0,9.5) rot=(0,0,1;0rad)
  Support = -> [Pocket]
  sketch-geometry (2):
    g0: Circle CenterX=13.5735 CenterY=-4.65 CenterZ=0 NormalX=0 NormalY=0 NormalZ=1 AngleXU=0 Radius=2
    g1: LineSegment StartX=13.5735 StartY=5.5 StartZ=0 EndX=13.5735 EndY=-14.8 EndZ=0
  constraints (7):
    c: Diameter(g0) = 4
    c: PointOnObject(g1,g-4)
    c: PointOnObject(g1,g-3)
    c: Vertical(g1)
    c: Symmetric(g1,g1,g0)
    c: DistanceX(g1,g-3) = 10.3265  'MagnetCenterToEdge'
    c: DistanceX(g0,g-5) = 4  'ActiveStartToBusDistance'
FEATURE [PartDesign::Pocket] Pocket001
  BaseFeature = -> Pocket
  Direction = (0,0,-1)
  Length = 8.5
  Length2 = 5
  Profile = -> Sketch003
  ReferenceAxis = -> Sketch003 [N_Axis]
  Type = 0
  expr: Length = <<Pad>>.Length + Pad001.Length - 1 mm
FEATURE [Sketcher::SketchObject] Sketch004
  ExternalGeometry = -> [Pocket001]
  FullyConstrained = true
  MapMode = 5
  Placement = pos=(0,0,1) rot=(0,0,1;0rad)
  Support = -> [Pocket001]
  sketch-geometry (1):
    g0: Circle CenterX=9.45 CenterY=2.5 CenterZ=0 NormalX=0 NormalY=0 NormalZ=1 AngleXU=0 Radius=1.5
  constraints (2):
    c: Coincident(g0,g-3)
    c: Diameter(g0) = 3
FEATURE [PartDesign::Pocket] Pocket002
  BaseFeature = -> Pocket001
  Direction = (0,0,-1)
  Length = 5
  Length2 = 5
  Profile = -> Sketch004
  ReferenceAxis = -> Sketch004 [N_Axis]
  Type = 1
FEATURE [Sketcher::SketchObject] Sketch005
  ExternalGeometry = -> [Pocket002]
  FullyConstrained = true
  MapMode = 5
  Placement = pos=(0,0,9.5) rot=(0,0,1;0rad)
  Support = -> [Pocket002]
  expr: .Constraints.Rad = <<OmniballConnector_7945>>#<<Sketch>>.Constraints.TopRad
  expr: Constraints[10] = .Constraints.Rad
  expr: Constraints[11] = .Constraints.Rad
  expr: Constraints[12] = .Constraints.Rad
  expr: Constraints[13] = .Constraints.Rad
  expr: Constraints[8] = .Constraints.Rad
  expr: Constraints[9] = .Constraints.Rad
  sketch-geometry (11):
    g0: Circle CenterX=17.5735 CenterY=-5.65 CenterZ=0 NormalX=0 NormalY=0 NormalZ=1 AngleXU=0 Radius=1.4986
    g1: Circle CenterX=17.5735 CenterY=-2.15 CenterZ=0 NormalX=0 NormalY=0 NormalZ=1 AngleXU=0 Radius=1.4986
    g2: Circle CenterX=20.6046 CenterY=-7.4 CenterZ=0 NormalX=0 NormalY=0 NormalZ=1 AngleXU=0 Radius=1.4986
    g3: Circle CenterX=17.5735 CenterY=-12.65 CenterZ=0 NormalX=0 NormalY=0 NormalZ=1 AngleXU=0 Radius=1.4986
    g4: Circle CenterX=20.6046 CenterY=-10.9 CenterZ=0 NormalX=0 NormalY=0 NormalZ=1 AngleXU=0 Radius=1.4986
    g5: Circle CenterX=17.5735 CenterY=-9.15 CenterZ=0 NormalX=0 NormalY=0 NormalZ=1 AngleXU=0 Radius=1.4986
    g6: Circle CenterX=13.5735 CenterY=-4.65 CenterZ=0 NormalX=0 NormalY=0 NormalZ=1 AngleXU=0 Radius=1.4986
    g7: LineSegment StartX=5 StartY=-0.6514 StartZ=0 EndX=23.9 EndY=-0.6514 EndZ=0
    g8: LineSegment StartX=23.9 StartY=-0.6514 StartZ=0 EndX=23.9 EndY=-14.8 EndZ=0
    g9: LineSegment StartX=23.9 StartY=-14.8 StartZ=0 EndX=5 EndY=-14.8 EndZ=0
    g10: LineSegment StartX=5 StartY=-14.8 StartZ=0 EndX=5 EndY=-0.6514 EndZ=0
  constraints (24):
    c: Coincident(g0,g-3)
    c: Coincident(g1,g-4)
    c: Coincident(g2,g-6)
    c: Coincident(g3,g-7)
    c: Coincident(g4,g-5)
    c: Coincident(g5,g-8)
    c: Coincident(g6,g-9)
    c: Diameter(g0) = 2.9972  'Rad'
    c: Diameter(g1) = 2.9972
    c: Diameter(g2) = 2.9972
    c: Diameter(g4) = 2.9972
    c: Diameter(g3) = 2.9972
    c: Diameter(g5) = 2.9972
    c: Diameter(g6) = 2.9972
    c: Coincident(g7,g8)
    c: Coincident(g8,g9)
    c: Coincident(g9,g10)
    c: Coincident(g10,g7)
    c: Horizontal(g7)
    c: Vertical(g8)
    c: Vertical(g10)
    c: Coincident(g9,g-11)
    c: Coincident(g8,g-10)
    c: Tangent(g7,g1)
FEATURE [PartDesign::Pocket] Pocket003
  BaseFeature = -> Pocket002
  Direction = (0,0,-1)
  Length = 4.1246
  Length2 = 5
  Profile = -> Sketch005
  ReferenceAxis = -> Sketch005 [N_Axis]
  Type = 0
  expr: Length = <<Pad>>.Length + <<Pad001>>.Length - (0.236 in + 0.015 in - <<Datasheet>>#<<mgn9c>>.Dim_H1 / 2)
FEATURE [PartDesign::Body] Body  label="SlideConnector"
  Group = -> [Binder,Binder001,Sketch,Pad,Binder002,Binder003,Sketch001,Pad001,Sketch002,Pocket,Sketch003,Pocket001,Sketch004,Pocket002,Sketch005,Pocket003]
  Origin = -> Origin
  Tip = -> Pocket003
---- part parts/OmniballConnector/OmniballConnector_7945.FCStd = doc fcstd_624c93e8ac9b ----
FCSTD DOCUMENT  (FreeCAD 0.21R33668 +26 (Git))
Label: OmniballConnector_7945
License: All rights reserved
LicenseURL: http://en.wikipedia.org/wiki/All_rights_reserved
objects: Sketcher::SketchObject×4, PartDesign::Pad×3, PartDesign::Revolution×1, PartDesign::Body×1
note: 13 computed .brp shape members not serialized (recipe doc carries the construction recipe); baked Part::Feature solids carry a one-line shape summary decoded from their .brp

FEATURE [Sketcher::SketchObject] Sketch
  FullyConstrained = true
  MapMode = 5
  Support = -> [XY_Plane]
  expr: .Constraints.TopRad = 0.118 in
  sketch-geometry (1):
    g0: Circle CenterX=0 CenterY=0 CenterZ=0 NormalX=0 NormalY=0 NormalZ=1 AngleXU=0 Radius=1.4986
  constraints (2):
    c: Coincident(g0,g-1)
    c: Diameter(g0) = 2.9972  'TopRad'
FEATURE [PartDesign::Pad] Pad
  Direction = (0,0,1)
  Length = 0.762
  Length2 = 10
  Profile = -> Sketch
  ReferenceAxis = -> Sketch [N_Axis]
  Type = 0
  expr: Length = 0.03 in
FEATURE [Sketcher::SketchObject] Sketch001
  FullyConstrained = true
  MapMode = 5
  Placement = pos=(0,0,0.762) rot=(0,0,1;0rad)
  Support = -> [Pad]
  expr: Constraints[1] = 0.107 in
  sketch-geometry (1):
    g0: Circle CenterX=0 CenterY=0 CenterZ=0 NormalX=0 NormalY=0 NormalZ=1 AngleXU=0 Radius=1.3589
  constraints (2):
    c: Coincident(g0,g-1)
    c: Diameter(g0) = 2.7178
FEATURE [PartDesign::Pad] Pad001
  BaseFeature = -> Pad
  Direction = (0,0,1)
  Length = 0.7112
  Length2 = 10
  Profile = -> Sketch001
  ReferenceAxis = -> Sketch001 [N_Axis]
  Type = 0
  expr: Length = 0.028 in
FEATURE [Sketcher::SketchObject] Sketch002
  FullyConstrained = true
  MapMode = 5
  Placement = pos=(0,0,1.4732) rot=(0,0,1;0rad)
  Support = -> [Pad001]
  expr: .Constraints.Smallest_Radius = 0.102 in
  sketch-geometry (1):
    g0: Circle CenterX=0 CenterY=0 CenterZ=0 NormalX=0 NormalY=0 NormalZ=1 AngleXU=0 Radius=1.2954
  constraints (2):
    c: Coincident(g0,g-1)
    c: Diameter(g0) = 2.5908  'Smallest_Radius'
FEATURE [PartDesign::Pad] Pad002
  BaseFeature = -> Pad001
  Direction = (0,0,1)
  Length = 4.5212
  Length2 = 10
  Profile = -> Sketch002
  ReferenceAxis = -> Sketch002 [N_Axis]
  Type = 0
  expr: Length = 0.236 in - 0.058 in
FEATURE [Sketcher::SketchObject] Sketch003
  FullyConstrained = true
  MapMode = 5
  Placement = pos=(0,0,5.9944) rot=(0,0,1;0rad)
  Support = -> [Pad002]
  expr: Constraints[3] = 0.091 in / 2
  sketch-geometry (2):
    g0: ArcOfCircle CenterX=0 CenterY=0 CenterZ=0 NormalX=0 NormalY=0 NormalZ=1 AngleXU=0 Radius=1.1557 StartAngle=4.71239 EndAngle=7.85398
    g1: LineSegment StartX=4e-16 StartY=1.1557 StartZ=0 EndX=-2e-16 EndY=-1.1557 EndZ=0
  constraints (6):
    c: Coincident(g0,g-1)
    c: PointOnObject(g0,g-2)
    c: PointOnObject(g0,g-2)
    c: Radius(g0) = 1.1557
    c: Coincident(g1,g0)
    c: Coincident(g1,g0)
FEATURE [PartDesign::Revolution] Revolution
  Angle = 180
  Axis = (0,1,0)
  Base = (0,0,5.9944)
  BaseFeature = -> Pad002
  Profile = -> Sketch003
  ReferenceAxis = -> Sketch003 [V_Axis]
  Reversed = true
FEATURE [PartDesign::Body] Body  label="7945"
  Group = -> [Sketch,Pad,Sketch001,Pad001,Sketch002,Pad002,Sketch003,Revolution]
  Origin = -> Origin
  Tip = -> Revolution
